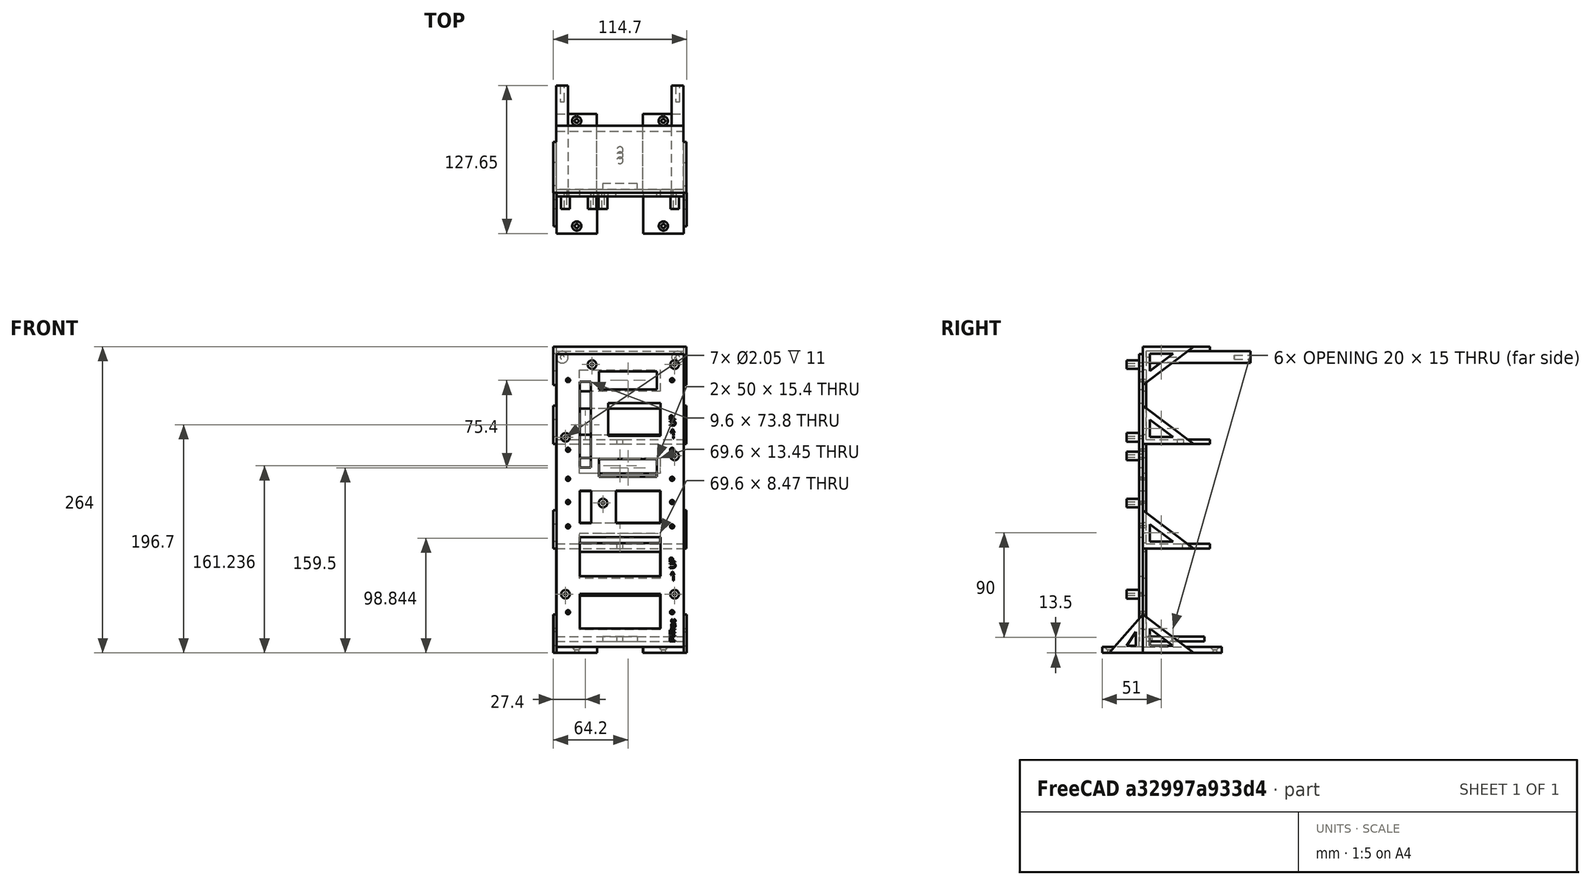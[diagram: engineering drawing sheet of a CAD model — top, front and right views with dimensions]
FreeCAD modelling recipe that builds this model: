
FCSTD DOCUMENT  (FreeCAD 1.0R39109 (Git))
Label: Tower
License: All rights reserved
LicenseURL: http://en.wikipedia.org/wiki/All_rights_reserved
objects: Sketcher::SketchObject×17, PartDesign::Pad×9, PartDesign::Plane×9, PartDesign::Pocket×5, PartDesign::Hole×3, PartDesign::Mirrored×2, PartDesign::Body×2, App::Link×1, Part::Part2DObjectPython×1, App::Part×1
note: 101 computed .brp shape members not serialized (recipe doc carries the construction recipe); baked Part::Feature solids carry a one-line shape summary decoded from their .brp
EXTERNAL_REF file=../Master Document.FCStd obj=Spreadsheet

FEATURE [App::Link] Link  label="Monitor Chassis Parameters"
  LinkedObject = -> <external ../Master Document.FCStd>#Spreadsheet
FEATURE [Sketcher::SketchObject] Sketch  label="Backplate Sketch"
  ArcFitTolerance = 1e-06
  AttachmentSupport = -> [XZ_Plane001]
  FullyConstrained = true
  MakeInternals = false
  MapMode = 5
  Placement = pos=(0,0,0) rot=(1,0,0;1.5708rad)
  expr: Constraints[107] = <<Monitor Chassis Parameters>>.GSBackPlateMinimumSpanWidth
  expr: Constraints[108] = <<Monitor Chassis Parameters>>.GSBackPlateMinimumSpanWidth - 8
  expr: Constraints[109] = <<Monitor Chassis Parameters>>.GSBackPlateMinimumSpanWidth - 5
  expr: Constraints[10] = <<Monitor Chassis Parameters>>.GSComputeBoardWidth / 2 - <<Monitor Chassis Parameters>>.GSBackPlateTopInnerHoleInsetFromSide
  expr: Constraints[118] = 30
  expr: Constraints[119] = <<Monitor Chassis Parameters>>.GSBackPlateMiddleRightHoleHeight
  expr: Constraints[11] = <<Monitor Chassis Parameters>>.GSBackPlateBoltDiameter
  expr: Constraints[120] = <<Monitor Chassis Parameters>>.GSBackPlateTopHolesHeight
  expr: Constraints[122] = <<Monitor Chassis Parameters>>.GSBackPlateMiddleHoleHeight
  expr: Constraints[123] = <<Monitor Chassis Parameters>>.GSBackPlateBottomHoleHeight
  expr: Constraints[126] = <<Monitor Chassis Parameters>>.GSBackPlateLengthIncrement
  expr: Constraints[12] = <<Monitor Chassis Parameters>>.GSComputeBoardWidth / 2 - <<Monitor Chassis Parameters>>.GSBackPlateOuterHolesInsetFromSide
  expr: Constraints[130] = <<Monitor Chassis Parameters>>.GSBackPlateMinimumSpanWidth
  expr: Constraints[131] = <<Monitor Chassis Parameters>>.GSBackPlateMinimumSpanWidth + 4
  expr: Constraints[132] = <<Monitor Chassis Parameters>>.GSBackPlateMinimumSpanWidth
  expr: Constraints[133] = <<Monitor Chassis Parameters>>.GSBackPlateMinimumSpanWidth - 5
  expr: Constraints[134] = <<Monitor Chassis Parameters>>.GSBackPlateWidth
  expr: Constraints[135] = <<Monitor Chassis Parameters>>.GSBackPlateHeight
  expr: Constraints[136] = <<Monitor Chassis Parameters>>.GSBackPlateMiddleLeftHoleHeight
  expr: Constraints[138] = <<Monitor Chassis Parameters>>.GSBackPlateBoltDiameter
  expr: Constraints[13] = <<Monitor Chassis Parameters>>.GSBackPlateBoltDiameter
  expr: Constraints[14] = <<Monitor Chassis Parameters>>.GSComputeBoardWidth / 2 - <<Monitor Chassis Parameters>>.GSBackPlateOuterHolesInsetFromSide
  expr: Constraints[150] = <<Monitor Chassis Parameters>>.GSBackPlateVerticalOffset
  expr: Constraints[15] = <<Monitor Chassis Parameters>>.GSBackPlateBoltDiameter
  expr: Constraints[17] = <<Monitor Chassis Parameters>>.GSComputeBoardWidth / 2 - <<Monitor Chassis Parameters>>.GSBackPlateOuterHolesInsetFromSide
  expr: Constraints[18] = <<Monitor Chassis Parameters>>.GSBackPlateBoltDiameter
  expr: Constraints[19] = <<Monitor Chassis Parameters>>.GSBackPlateWidth / 2 - <<Monitor Chassis Parameters>>.GSBackPlateMiddleHoleOffsetFromLeftSide
  expr: Constraints[20] = <<Monitor Chassis Parameters>>.GSBackPlateBoltDiameter
  expr: Constraints[21] = <<Monitor Chassis Parameters>>.GSBackPlateBoltDiameter
  expr: Constraints[25] = <<Monitor Chassis Parameters>>.GSBackPlateWidthIncrement
  expr: Constraints[66] = 50
  expr: Constraints[68] = 45
  expr: Constraints[73] = <<Monitor Chassis Parameters>>.GSBackPlateMinimumSpanWidth
  expr: Constraints[7] = <<Monitor Chassis Parameters>>.GSComputeBoardHeight
  expr: Constraints[82] = <<Monitor Chassis Parameters>>.GSBackPlateMinimumSpanWidth - 5
  expr: Constraints[8] = <<Monitor Chassis Parameters>>.GSComputeBoardWidth
  expr: Constraints[9] = <<Monitor Chassis Parameters>>.GSComputeBoardWidth / 2
  sketch-geometry (51):
    g0: LineSegment [constr] StartX=-50.8 StartY=20 StartZ=0 EndX=50.8 EndY=20 EndZ=0
    g1: LineSegment [constr] StartX=50.8 StartY=20 StartZ=0 EndX=50.8 EndY=248.6 EndZ=0
    g2: LineSegment [constr] StartX=50.8 StartY=248.6 StartZ=0 EndX=-50.8 EndY=248.6 EndZ=0
    g3: LineSegment [constr] StartX=-50.8 StartY=248.6 StartZ=0 EndX=-50.8 EndY=20 EndZ=0
    g4: Circle CenterX=-24.13 CenterY=243.52 CenterZ=0 NormalX=0 NormalY=0 NormalZ=1 AngleXU=0 Radius=1.4
    g5: Circle CenterX=46.99 CenterY=243.52 CenterZ=0 NormalX=0 NormalY=0 NormalZ=1 AngleXU=0 Radius=1.4
    g6: Circle CenterX=-46.99 CenterY=45.5 CenterZ=0 NormalX=0 NormalY=0 NormalZ=1 AngleXU=0 Radius=1.4
    g7: Circle CenterX=46.99 CenterY=45.5 CenterZ=0 NormalX=0 NormalY=0 NormalZ=1 AngleXU=0 Radius=1.4
    g8: Circle CenterX=-14.668 CenterY=124.14 CenterZ=0 NormalX=0 NormalY=0 NormalZ=1 AngleXU=0 Radius=1.4
    g9: Circle CenterX=-46.99 CenterY=180.78 CenterZ=0 NormalX=0 NormalY=0 NormalZ=1 AngleXU=0 Radius=1.4
    g10: Circle CenterX=46.99 CenterY=164.78 CenterZ=0 NormalX=0 NormalY=0 NormalZ=1 AngleXU=0 Radius=1.4
    g11: LineSegment StartX=-54.8 StartY=252.6 StartZ=0 EndX=-54.8 EndY=16 EndZ=0
    g12: LineSegment [constr] StartX=-54.8 StartY=16 StartZ=0 EndX=54.8 EndY=16 EndZ=0
    g13: LineSegment StartX=31.8 StartY=162.2 StartZ=0 EndX=-18.2 EndY=162.2 EndZ=0
    g14: LineSegment StartX=-18.2 StartY=162.2 StartZ=0 EndX=-18.2 EndY=146.8 EndZ=0
    g15: LineSegment StartX=-18.2 StartY=146.8 StartZ=0 EndX=31.8 EndY=146.8 EndZ=0
    g16: LineSegment StartX=31.8 StartY=146.8 StartZ=0 EndX=31.8 EndY=162.2 EndZ=0
    g17: LineSegment StartX=34.8 StartY=106.8 StartZ=0 EndX=-3.7 EndY=106.8 EndZ=0
    g18: LineSegment StartX=-3.7 StartY=106.8 StartZ=0 EndX=-3.7 EndY=134.8 EndZ=0
    g19: LineSegment StartX=-3.7 StartY=134.8 StartZ=0 EndX=34.8 EndY=134.8 EndZ=0
    g20: LineSegment StartX=34.8 StartY=134.8 StartZ=0 EndX=34.8 EndY=106.8 EndZ=0
    g21: LineSegment StartX=31.8 StartY=237.6 StartZ=0 EndX=-18.2 EndY=237.6 EndZ=0
    g22: LineSegment StartX=-18.2 StartY=237.6 StartZ=0 EndX=-18.2 EndY=222.2 EndZ=0
    g23: LineSegment StartX=-18.2 StartY=222.2 StartZ=0 EndX=31.8 EndY=222.2 EndZ=0
    g24: LineSegment StartX=31.8 StartY=222.2 StartZ=0 EndX=31.8 EndY=237.6 EndZ=0
    g25: LineSegment StartX=34.8 StartY=182.2 StartZ=0 EndX=-10.2 EndY=182.2 EndZ=0
    g26: LineSegment StartX=-10.2 StartY=182.2 StartZ=0 EndX=-10.2 EndY=210.2 EndZ=0
    g27: LineSegment StartX=-10.2 StartY=210.2 StartZ=0 EndX=34.8 EndY=210.2 EndZ=0
    g28: LineSegment StartX=34.8 StartY=210.2 StartZ=0 EndX=34.8 EndY=182.2 EndZ=0
    g29: LineSegment StartX=-34.8 StartY=228.6 StartZ=0 EndX=-34.8 EndY=154.8 EndZ=0
    g30: LineSegment StartX=-34.8 StartY=154.8 StartZ=0 EndX=-25.2 EndY=154.8 EndZ=0
    g31: LineSegment StartX=-25.2 StartY=154.8 StartZ=0 EndX=-25.2 EndY=228.6 EndZ=0
    g32: LineSegment StartX=-25.2 StartY=228.6 StartZ=0 EndX=-34.8 EndY=228.6 EndZ=0
    g33: LineSegment StartX=-34.8 StartY=134.8 StartZ=0 EndX=-34.8 EndY=106.8 EndZ=0
    g34: LineSegment StartX=-34.8 StartY=106.8 StartZ=0 EndX=-24.668 EndY=106.8 EndZ=0
    g35: LineSegment StartX=-24.668 StartY=106.8 StartZ=0 EndX=-24.668 EndY=134.8 EndZ=0
    g36: LineSegment StartX=-24.668 StartY=134.8 StartZ=0 EndX=-34.8 EndY=134.8 EndZ=0
    g37: LineSegment StartX=-34.8 StartY=94.8 StartZ=0 EndX=-34.8 EndY=61 EndZ=0
    g38: LineSegment StartX=-34.8 StartY=61 StartZ=0 EndX=34.8 EndY=61 EndZ=0
    g39: LineSegment StartX=34.8 StartY=61 StartZ=0 EndX=34.8 EndY=94.8 EndZ=0
    g40: LineSegment StartX=34.8 StartY=94.8 StartZ=0 EndX=-34.8 EndY=94.8 EndZ=0
    g41: LineSegment StartX=-34.8 StartY=46 StartZ=0 EndX=-34.8 EndY=16 EndZ=0
    g42: LineSegment StartX=-34.8 StartY=16 StartZ=0 EndX=34.8 EndY=16 EndZ=0
    g43: LineSegment StartX=34.8 StartY=16 StartZ=0 EndX=34.8 EndY=46 EndZ=0
    g44: LineSegment StartX=34.8 StartY=46 StartZ=0 EndX=-34.8 EndY=46 EndZ=0
    g45: LineSegment StartX=54.8 StartY=16 StartZ=0 EndX=54.8 EndY=252.6 EndZ=0
    g46: LineSegment StartX=-54.8 StartY=252.6 StartZ=0 EndX=54.8 EndY=252.6 EndZ=0
    g47: LineSegment StartX=-54.8 StartY=16 StartZ=0 EndX=-54.8 EndY=0 EndZ=0
    g48: LineSegment StartX=-54.8 StartY=0 StartZ=0 EndX=54.8 EndY=0 EndZ=0
    g49: LineSegment StartX=54.8 StartY=0 StartZ=0 EndX=54.8 EndY=16 EndZ=0
    g50: LineSegment [constr] StartX=54.8 StartY=16 StartZ=0 EndX=-54.8 EndY=16 EndZ=0
  constraints (152):
    c: Coincident(g0,g1)
    c: Coincident(g1,g2)
    c: Coincident(g2,g3)
    c: Coincident(g3,g0)
    c: Horizontal(g2)
    c: Vertical(g1)
    c: Vertical(g3)
    c: DistanceY(g0,g2) = 228.6
    c: DistanceX(g0,g0) = 101.6
    c: DistanceX(g0,g-1) = 50.8
    c: DistanceX(g4,g-1) = 24.13
    c: Diameter(g4) = 2.8
    c: DistanceX(g-1,g5) = 46.99
    c: Diameter(g6) = 2.8
    c: DistanceX(g6,g-1) = 46.99
    c: Diameter(g7) = 2.8
    c: Horizontal(g7,g6)
    c: DistanceX(g-1,g7) = 46.99
    c: Diameter(g8) = 2.8
    c: DistanceX(g8,g-1) = 14.668
    c: Diameter(g9) = 2.8
    c: Diameter(g10) = 2.8
    c: Coincident(g11,g12)
    c: Vertical(g11)
    c: Horizontal(g12)
    c: DistanceX(g11,g0) = 4
    c: Horizontal(g0)
    c: Vertical(g6,g9)
    c: Coincident(g13,g14)
    c: Coincident(g14,g15)
    c: Coincident(g15,g16)
    c: Coincident(g16,g13)
    c: Horizontal(g13)
    c: Horizontal(g15)
    c: Vertical(g14)
    c: Vertical(g16)
    c: Coincident(g17,g18)
    c: Coincident(g18,g19)
    c: Coincident(g19,g20)
    c: Coincident(g20,g17)
    c: Horizontal(g17)
    c: Horizontal(g19)
    c: Vertical(g18)
    c: Vertical(g20)
    c: DistanceX(g13,g13) = 50
    c: DistanceY(g14,g13) = 15.4
    c: DistanceX(g18,g19) = 38.5
    c: DistanceY(g17,g18) = 28
    c: DistanceY(g19,g15) = 12
    c: DistanceX(g15,g19) = 3
    c: Coincident(g21,g22)
    c: Coincident(g22,g23)
    c: Coincident(g23,g24)
    c: Coincident(g24,g21)
    c: Horizontal(g21)
    c: Horizontal(g23)
    c: Vertical(g22)
    c: Vertical(g24)
    c: Coincident(g25,g26)
    c: Coincident(g26,g27)
    c: Coincident(g27,g28)
    c: Coincident(g28,g25)
    c: Horizontal(g25)
    c: Horizontal(g27)
    c: Vertical(g26)
    c: Vertical(g28)
    c: DistanceX(g21,g21) = 50
    c: DistanceY(g22,g21) = 15.4
    c: DistanceX(g26,g27) = 45
    c: DistanceY(g25,g26) = 28
    c: DistanceY(g27,g23) = 12
    c: DistanceX(g23,g27) = 3
    c: Vertical(g19,g25)
    c: DistanceY(g13,g25) = 20
    c: Coincident(g29,g30)
    c: Coincident(g30,g31)
    c: Coincident(g31,g32)
    c: Coincident(g32,g29)
    c: Vertical(g29)
    c: Vertical(g31)
    c: Horizontal(g30)
    c: Horizontal(g32)
    c: DistanceX(g31,g26) = 15
    c: Coincident(g33,g34)
    c: Coincident(g34,g35)
    c: Coincident(g35,g36)
    c: Coincident(g36,g33)
    c: Vertical(g33)
    c: Vertical(g35)
    c: Horizontal(g34)
    c: Horizontal(g36)
    c: Coincident(g37,g38)
    c: Coincident(g38,g39)
    c: Coincident(g39,g40)
    c: Coincident(g40,g37)
    c: Vertical(g37)
    c: Vertical(g39)
    c: Horizontal(g38)
    c: Horizontal(g40)
    c: Coincident(g41,g42)
    c: Coincident(g42,g43)
    c: Coincident(g43,g44)
    c: Coincident(g44,g41)
    c: Vertical(g41)
    c: Vertical(g43)
    c: Horizontal(g42)
    c: Horizontal(g44)
    c: DistanceY(g33,g29) = 20
    c: DistanceY(g37,g33) = 12
    c: DistanceY(g41,g37) = 15
    c: Vertical(g29,g33)
    c: Vertical(g33,g37)
    c: Vertical(g37,g41)
    c: Vertical(g17,g39)
    c: Vertical(g39,g43)
    c: Horizontal(g35,g18)
    c: DistanceX(g35,g8) = 10
    c: Horizontal(g34,g17)
    c: DistanceY(g41,g41) = 30
    c: DistanceY(g0,g10) = 144.78
    c: DistanceY(g0,g4) = 223.52
    c: Horizontal(g5,g4)
    c: DistanceY(g0,g8) = 104.14
    c: DistanceY(g0,g6) = 25.5
    c: Coincident(g45,g12)
    c: Vertical(g45)
    c: DistanceY(g1,g45) = 4
    c: Horizontal(g11,g45)
    c: Coincident(g46,g11)
    c: Coincident(g46,g45)
    c: DistanceX(g11,g29) = 20
    c: DistanceY(g29,g11) = 24
    c: DistanceX(g27,g45) = 20
    c: DistanceY(g21,g45) = 15
    c: DistanceX(g11,g12) = 109.6
    c: DistanceY(g11,g11) = 236.6
    c: DistanceY(g0,g9) = 160.78
    c: Vertical(g7,g10)
    c: Diameter(g5) = 2.8
    c: Coincident(g47,g48)
    c: Coincident(g48,g49)
    c: Coincident(g49,g50)
    c: Coincident(g50,g47)
    c: Vertical(g47)
    c: Vertical(g49)
    c: Horizontal(g48)
    c: Horizontal(g50)
    c: Coincident(g47,g11)
    c: Horizontal(g48,g-1)
    c: Vertical(g49,g12)
    c: DistanceY(g-1,g0) = 20
    c: Horizontal(g41,g11)
FEATURE [PartDesign::Pad] Pad  label="Backplate Pad"
  Direction = (0,-1,2e-16)
  Length = 3
  Length2 = 10
  Placement = pos=(0,0,0) rot=(1,0,0;1.5708rad)
  Profile = -> Sketch
  ReferenceAxis = -> Sketch [N_Axis]
  Reversed = true
  Suppressed = false
  Type = 0
  expr: Length = <<Monitor Chassis Parameters>>.GSBackPlateThickness
FEATURE [Sketcher::SketchObject] Sketch001  label="Backplate Risers Sketch"
  ArcFitTolerance = 1e-06
  AttachmentSupport = -> [XZ_Plane001]
  FullyConstrained = true
  MakeInternals = false
  MapMode = 5
  Placement = pos=(0,0,0) rot=(1,0,0;1.5708rad)
  expr: Constraints[10] = <<Monitor Chassis Parameters>>.GSM2_5TappingScrewHoleDiameter
  expr: Constraints[11] = <<Monitor Chassis Parameters>>.GSM2_5TappingScrewHoleDiameter
  expr: Constraints[12] = <<Monitor Chassis Parameters>>.GSComputeBoardWidth / 2 - <<Monitor Chassis Parameters>>.GSBackPlateOuterHolesInsetFromSide
  expr: Constraints[13] = <<Monitor Chassis Parameters>>.GSM2_5TappingScrewHoleDiameter
  expr: Constraints[14] = <<Monitor Chassis Parameters>>.GSComputeBoardWidth / 2 - <<Monitor Chassis Parameters>>.GSBackPlateOuterHolesInsetFromSide
  expr: Constraints[15] = <<Monitor Chassis Parameters>>.GSM2_5TappingScrewHoleDiameter
  expr: Constraints[16] = <<Monitor Chassis Parameters>>.GSComputeBoardWidth / 2 - <<Monitor Chassis Parameters>>.GSBackPlateOuterHolesInsetFromSide
  expr: Constraints[17] = <<Monitor Chassis Parameters>>.GSM2_5TappingScrewHoleDiameter
  expr: Constraints[18] = <<Monitor Chassis Parameters>>.GSBackPlateWidth / 2 - <<Monitor Chassis Parameters>>.GSBackPlateMiddleHoleOffsetFromLeftSide
  expr: Constraints[19] = <<Monitor Chassis Parameters>>.GSM2_5TappingScrewHoleDiameter
  expr: Constraints[20] = <<Monitor Chassis Parameters>>.GSM2_5TappingScrewHoleDiameter
  expr: Constraints[25] = <<Monitor Chassis Parameters>>.GSBackPlateScrewHoleDiameter + 2 * <<Monitor Chassis Parameters>>.GSBackPlateStandoffWallThickness
  expr: Constraints[27] = <<Monitor Chassis Parameters>>.GSBackPlateScrewHoleDiameter + 2 * <<Monitor Chassis Parameters>>.GSBackPlateStandoffWallThickness
  expr: Constraints[33] = <<Monitor Chassis Parameters>>.GSBackPlateScrewHoleDiameter + 2 * <<Monitor Chassis Parameters>>.GSBackPlateStandoffWallThickness
  expr: Constraints[34] = <<Monitor Chassis Parameters>>.GSBackPlateScrewHoleDiameter + 2 * <<Monitor Chassis Parameters>>.GSBackPlateStandoffWallThickness
  expr: Constraints[35] = <<Monitor Chassis Parameters>>.GSBackPlateScrewHoleDiameter + 2 * <<Monitor Chassis Parameters>>.GSBackPlateStandoffWallThickness
  expr: Constraints[36] = <<Monitor Chassis Parameters>>.GSBackPlateScrewHoleDiameter + 2 * <<Monitor Chassis Parameters>>.GSBackPlateStandoffWallThickness
  expr: Constraints[37] = <<Monitor Chassis Parameters>>.GSBackPlateScrewHoleDiameter + 2 * <<Monitor Chassis Parameters>>.GSBackPlateStandoffWallThickness
  expr: Constraints[39] = <<Monitor Chassis Parameters>>.GSBackPlateMiddleLeftHoleHeight
  expr: Constraints[40] = <<Monitor Chassis Parameters>>.GSBackPlateBottomHoleHeight
  expr: Constraints[42] = <<Monitor Chassis Parameters>>.GSBackPlateMiddleHoleHeight
  expr: Constraints[43] = <<Monitor Chassis Parameters>>.GSBackPlateTopHolesHeight
  expr: Constraints[44] = <<Monitor Chassis Parameters>>.GSBackPlateMiddleRightHoleHeight
  expr: Constraints[45] = <<Monitor Chassis Parameters>>.GSBackPlateVerticalOffset
  expr: Constraints[6] = <<Monitor Chassis Parameters>>.GSComputeBoardHeight
  expr: Constraints[7] = <<Monitor Chassis Parameters>>.GSComputeBoardWidth
  expr: Constraints[8] = <<Monitor Chassis Parameters>>.GSComputeBoardWidth / 2
  expr: Constraints[9] = 0.5 * <<Monitor Chassis Parameters>>.GSComputeBoardWidth - <<Monitor Chassis Parameters>>.GSBackPlateTopInnerHoleInsetFromSide
  sketch-geometry (18):
    g0: LineSegment [constr] StartX=-50.8 StartY=20 StartZ=0 EndX=50.8 EndY=20 EndZ=0
    g1: LineSegment [constr] StartX=50.8 StartY=20 StartZ=0 EndX=50.8 EndY=248.6 EndZ=0
    g2: LineSegment [constr] StartX=50.8 StartY=248.6 StartZ=0 EndX=-50.8 EndY=248.6 EndZ=0
    g3: LineSegment [constr] StartX=-50.8 StartY=248.6 StartZ=0 EndX=-50.8 EndY=20 EndZ=0
    g4: Circle CenterX=-24.13 CenterY=243.52 CenterZ=0 NormalX=0 NormalY=0 NormalZ=1 AngleXU=0 Radius=1.025
    g5: Circle CenterX=46.99 CenterY=243.52 CenterZ=0 NormalX=0 NormalY=0 NormalZ=1 AngleXU=0 Radius=1.025
    g6: Circle CenterX=-46.99 CenterY=45.5 CenterZ=0 NormalX=0 NormalY=0 NormalZ=1 AngleXU=0 Radius=1.025
    g7: Circle CenterX=46.99 CenterY=45.5 CenterZ=0 NormalX=0 NormalY=0 NormalZ=1 AngleXU=0 Radius=1.025
    g8: Circle CenterX=-14.668 CenterY=124.14 CenterZ=0 NormalX=0 NormalY=0 NormalZ=1 AngleXU=0 Radius=1.025
    g9: Circle CenterX=-46.99 CenterY=180.78 CenterZ=0 NormalX=0 NormalY=0 NormalZ=1 AngleXU=0 Radius=1.025
    g10: Circle CenterX=46.99 CenterY=164.78 CenterZ=0 NormalX=0 NormalY=0 NormalZ=1 AngleXU=0 Radius=1.025
    g11: Circle CenterX=-24.13 CenterY=243.52 CenterZ=0 NormalX=0 NormalY=0 NormalZ=1 AngleXU=0 Radius=3.7
    g12: Circle CenterX=46.99 CenterY=243.52 CenterZ=0 NormalX=0 NormalY=0 NormalZ=1 AngleXU=0 Radius=3.7
    g13: Circle CenterX=-46.99 CenterY=180.78 CenterZ=0 NormalX=0 NormalY=0 NormalZ=1 AngleXU=0 Radius=3.7
    g14: Circle CenterX=46.99 CenterY=164.78 CenterZ=0 NormalX=0 NormalY=0 NormalZ=1 AngleXU=0 Radius=3.7
    g15: Circle CenterX=-14.668 CenterY=124.14 CenterZ=0 NormalX=0 NormalY=0 NormalZ=1 AngleXU=0 Radius=3.7
    g16: Circle CenterX=-46.99 CenterY=45.5 CenterZ=0 NormalX=0 NormalY=0 NormalZ=1 AngleXU=0 Radius=3.7
    g17: Circle CenterX=46.99 CenterY=45.5 CenterZ=0 NormalX=0 NormalY=0 NormalZ=1 AngleXU=0 Radius=3.7
  constraints (47):
    c: Coincident(g0,g1)
    c: Coincident(g1,g2)
    c: Coincident(g2,g3)
    c: Coincident(g3,g0)
    c: Vertical(g1)
    c: Vertical(g3)
    c: DistanceY(g0,g2) = 228.6
    c: DistanceX(g0,g0) = 101.6
    c: DistanceX(g0,g-1) = 50.8
    c: DistanceX(g4,g-1) = 24.13
    c: Diameter(g4) = 2.05
    c: Diameter(g5) = 2.05
    c: DistanceX(g-1,g5) = 46.99
    c: Diameter(g6) = 2.05
    c: DistanceX(g6,g-1) = 46.99
    c: Diameter(g7) = 2.05
    c: DistanceX(g-1,g7) = 46.99
    c: Diameter(g8) = 2.05
    c: DistanceX(g8,g-1) = 14.668
    c: Diameter(g9) = 2.05
    c: Diameter(g10) = 2.05
    c: Horizontal(g0)
    c: Vertical(g5,g10)
    c: Horizontal(g5,g4)
    c: Coincident(g11,g4)
    c: Diameter(g11) = 7.4
    c: Coincident(g12,g5)
    c: Diameter(g12) = 7.4
    c: Coincident(g13,g9)
    c: Coincident(g14,g10)
    c: Coincident(g15,g8)
    c: Coincident(g16,g6)
    c: Coincident(g17,g7)
    c: Diameter(g17) = 7.4
    c: Diameter(g16) = 7.4
    c: Diameter(g15) = 7.4
    c: Diameter(g14) = 7.4
    c: Diameter(g13) = 7.4
    c: Vertical(g9,g6)
    c: DistanceY(g0,g9) = 160.78
    c: DistanceY(g0,g6) = 25.5
    c: Horizontal(g7,g6)
    c: DistanceY(g0,g8) = 104.14
    c: DistanceY(g0,g4) = 223.52
    c: DistanceY(g0,g10) = 144.78
    c: DistanceY(g-1,g0) = 20
    c: Horizontal(g2,g1)
FEATURE [PartDesign::Pad] Pad001  label="Backplate Risers Pad"
  BaseFeature = -> Pad
  Direction = (0,-1,2e-16)
  Length = 11
  Length2 = 10
  Placement = pos=(0,0,0) rot=(1,0,0;1.5708rad)
  Profile = -> Sketch001
  ReferenceAxis = -> Sketch001 [N_Axis]
  Suppressed = false
  Type = 0
  expr: Length = <<Monitor Chassis Parameters>>.GSBackPlateStandoffHeight
FEATURE [Sketcher::SketchObject] Sketch002  label="Backplate Foot Sketch"
  ArcFitTolerance = 1e-06
  AttachmentSupport = -> [XZ_Plane001]
  FullyConstrained = true
  MakeInternals = false
  MapMode = 5
  Placement = pos=(0,0,0) rot=(1,0,0;1.5708rad)
  expr: Constraints[11] = <<Monitor Chassis Parameters>>.GSTowerFeetThickness
  expr: Constraints[21] = <<Monitor Chassis Parameters>>.GSTowerFeetThickness
  expr: Constraints[22] = <<Monitor Chassis Parameters>>.GSBackPlateFootWidth
  expr: Constraints[23] = 0.5 * <<Monitor Chassis Parameters>>.GSBackPlateWidth
  expr: Constraints[8] = <<Monitor Chassis Parameters>>.GSBackPlateFootWidth
  expr: Constraints[9] = 0.5 * <<Monitor Chassis Parameters>>.GSBackPlateWidth
  sketch-geometry (8):
    g0: LineSegment StartX=-54.8 StartY=-5 StartZ=0 EndX=-19.8 EndY=-5 EndZ=0
    g1: LineSegment StartX=-19.8 StartY=-5 StartZ=0 EndX=-19.8 EndY=0 EndZ=0
    g2: LineSegment StartX=-19.8 StartY=0 StartZ=0 EndX=-54.8 EndY=0 EndZ=0
    g3: LineSegment StartX=-54.8 StartY=0 StartZ=0 EndX=-54.8 EndY=-5 EndZ=0
    g4: LineSegment StartX=54.8 StartY=-5 StartZ=0 EndX=54.8 EndY=0 EndZ=0
    g5: LineSegment StartX=54.8 StartY=0 StartZ=0 EndX=19.8 EndY=0 EndZ=0
    g6: LineSegment StartX=19.8 StartY=0 StartZ=0 EndX=19.8 EndY=-5 EndZ=0
    g7: LineSegment StartX=19.8 StartY=-5 StartZ=0 EndX=54.8 EndY=-5 EndZ=0
  constraints (24):
    c: Coincident(g0,g1)
    c: Coincident(g1,g2)
    c: Coincident(g2,g3)
    c: Coincident(g3,g0)
    c: Horizontal(g0)
    c: Horizontal(g2)
    c: Vertical(g1)
    c: Vertical(g3)
    c: DistanceX(g2,g1) = 35
    c: DistanceX(g2,g-1) = 54.8
    c: Horizontal(g2,g-1)
    c: DistanceY(g0,g2) = 5
    c: Coincident(g4,g5)
    c: Coincident(g5,g6)
    c: Coincident(g6,g7)
    c: Coincident(g7,g4)
    c: Vertical(g4)
    c: Vertical(g6)
    c: Horizontal(g5)
    c: Horizontal(g7)
    c: Horizontal(g5,g-1)
    c: DistanceY(g4,g4) = 5
    c: DistanceX(g6,g4) = 35
    c: DistanceX(g-1,g4) = 54.8
FEATURE [PartDesign::Pad] Pad002  label="Backplate Foot Pad"
  BaseFeature = -> Pad001
  Direction = (0,-1,2e-16)
  Length = 32
  Length2 = 3
  Placement = pos=(0,0,0) rot=(1,0,0;1.5708rad)
  Profile = -> Sketch002
  ReferenceAxis = -> Sketch002 [N_Axis]
  Suppressed = false
  Type = 4
  expr: Length = <<Monitor Chassis Parameters>>.GSBackPlateFootLengthBackward
  expr: Length2 = <<Monitor Chassis Parameters>>.GSBackPlateThickness
FEATURE [Sketcher::SketchObject] Sketch003  label="Backplate Foot Screw Holes Sketch"
  ArcFitTolerance = 1e-06
  AttachmentSupport = -> [XY_Plane001]
  FullyConstrained = true
  MakeInternals = false
  MapMode = 5
  expr: Constraints[0] = 0.8 * <<Monitor Chassis Parameters>>.GSBackPlateFootLengthBackward
  expr: Constraints[1] = 0.5 * <<Monitor Chassis Parameters>>.GSBackPlateWidth - 0.5 * <<Monitor Chassis Parameters>>.GSBackPlateFootWidth
  expr: Constraints[2] = 0.5 * <<Monitor Chassis Parameters>>.GSBackPlateWidth - 0.5 * <<Monitor Chassis Parameters>>.GSBackPlateFootWidth
  expr: Constraints[3] = <<Monitor Chassis Parameters>>.GSTowerFeetScrewDiameter
  expr: Constraints[4] = <<Monitor Chassis Parameters>>.GSTowerFeetScrewDiameter
  sketch-geometry (2):
    g0: Circle CenterX=-37.3 CenterY=-25.6 CenterZ=0 NormalX=0 NormalY=0 NormalZ=1 AngleXU=0 Radius=1.7
    g1: Circle CenterX=37.3 CenterY=-25.6 CenterZ=0 NormalX=0 NormalY=0 NormalZ=1 AngleXU=0 Radius=1.7
  constraints (6):
    c: DistanceY(g0,g-1) = 25.6
    c: DistanceX(g0,g-1) = 37.3
    c: DistanceX(g-1,g1) = 37.3
    c: Diameter(g0) = 3.4
    c: Diameter(g1) = 3.4
    c: Horizontal(g1,g0)
FEATURE [PartDesign::Hole] Hole  label="Backplate Foot Screw Holes"
  BaseFeature = -> Pad002
  CustomThreadClearance = 0
  Depth = 25
  DepthType = 0
  Diameter = 3.4
  DrillForDepth = false
  DrillPoint = 1
  DrillPointAngle = 118
  HoleCutCountersinkAngle = 90
  HoleCutCustomValues = false
  HoleCutDepth = 0
  HoleCutDiameter = 8
  HoleCutType = 2
  ModelThread = false
  Placement = pos=(0,0,0) rot=(1,0,0;1.5708rad)
  Profile = -> Sketch003
  Suppressed = false
  Tapered = false
  TaperedAngle = 90
  ThreadClass = 0
  ThreadDepth = 25
  ThreadDepthType = 0
  ThreadDirection = 0
  ThreadFit = 0
  ThreadSize = 0
  ThreadType = 0
  Threaded = false
  UseCustomThreadClearance = false
  expr: Diameter = <<Monitor Chassis Parameters>>.GSTowerFeetScrewDiameter
  expr: HoleCutDiameter = <<Monitor Chassis Parameters>>.GSM4BoltCountersinkDiameter
FEATURE [PartDesign::Plane] DatumPlane
  AttachmentOffset = pos=(0,0,54.8) rot=(0,0,1;0rad)
  AttachmentSupport = -> [YZ_Plane001]
  Length = 60
  MapMode = 5
  Placement = pos=(54.8,0,0) rot=(0.57735,0.57735,0.57735;2.0944rad)
  ResizeMode = 0
  Width = 60
  expr: .AttachmentOffset.Base.z = 0.5 * <<Monitor Chassis Parameters>>.GSBackPlateWidth
FEATURE [Sketcher::SketchObject] Sketch004  label="Foot Support Corner Sketch"
  ArcFitTolerance = 1e-06
  AttachmentSupport = -> [DatumPlane]
  FullyConstrained = true
  MakeInternals = false
  MapMode = 5
  Placement = pos=(54.8,0,0) rot=(0.57735,0.57735,0.57735;2.0944rad)
  expr: Constraints[14] = <<Monitor Chassis Parameters>>.GSSideCornerCutoutInset
  expr: Constraints[15] = <<Monitor Chassis Parameters>>.GSSideCornerCutoutInset
  expr: Constraints[16] = 2.5 * <<Monitor Chassis Parameters>>.GSSideCornerCutoutInset
  expr: Constraints[17] = 2.5 * <<Monitor Chassis Parameters>>.GSSideCornerCutoutInset
  expr: Constraints[1] = <<Monitor Chassis Parameters>>.GSBackPlateThickness
  expr: Constraints[4] = <<Monitor Chassis Parameters>>.GSTowerFeetThickness
  expr: Constraints[7] = 0.9 * <<Monitor Chassis Parameters>>.GSBackPlateFootLengthBackward
  expr: Constraints[8] = 0.6 * <<Monitor Chassis Parameters>>.GSTowerFloorDepth
  sketch-geometry (6):
    g0: LineSegment StartX=-25.8 StartY=-5 StartZ=0 EndX=3 EndY=-5 EndZ=0
    g1: LineSegment StartX=3 StartY=28 StartZ=0 EndX=3 EndY=-5 EndZ=0
    g2: LineSegment StartX=-25.8 StartY=-5 StartZ=0 EndX=3 EndY=28 EndZ=0
    g3: LineSegment StartX=-10.8 StartY=1 StartZ=0 EndX=-3 EndY=13 EndZ=0
    g4: LineSegment StartX=-3 StartY=13 StartZ=0 EndX=-3 EndY=1 EndZ=0
    g5: LineSegment StartX=-10.8 StartY=1 StartZ=0 EndX=-3 EndY=1 EndZ=0
  constraints (18):
    c: Horizontal(g0)
    c: DistanceX(g-1,g0) = 3
    c: Coincident(g1,g0)
    c: Vertical(g1)
    c: DistanceY(g0,g-1) = 5
    c: Coincident(g2,g0)
    c: Coincident(g2,g1)
    c: DistanceX(g0,g0) = 28.8
    c: DistanceY(g0,g1) = 33
    c: Coincident(g4,g3)
    c: Vertical(g4)
    c: Coincident(g5,g3)
    c: Coincident(g5,g4)
    c: Horizontal(g5)
    c: DistanceY(g0,g4) = 6
    c: DistanceX(g4,g0) = 6
    c: DistanceX(g0,g3) = 15
    c: DistanceY(g3,g1) = 15
FEATURE [PartDesign::Pad] Pad003  label="Foot Support Corner Pad"
  BaseFeature = -> Hole
  Direction = (1,0,0)
  Length = 2.5
  Length2 = 10
  Placement = pos=(0,0,0) rot=(1,0,0;1.5708rad)
  Profile = -> Sketch004
  ReferenceAxis = -> Sketch004 [N_Axis]
  Suppressed = false
  Type = 0
  expr: Length = <<Monitor Chassis Parameters>>.GSSideCornerThickness
FEATURE [PartDesign::Mirrored] Mirrored  label="Foot Support Corner Mirrored"
  BaseFeature = -> Pad003
  MirrorPlane = -> YZ_Plane001
  Originals = -> [Pad003]
  Placement = pos=(0,0,0) rot=(1,0,0;1.5708rad)
  Suppressed = false
  TransformMode = 0
FEATURE [PartDesign::Plane] DatumPlane001
  AttachmentOffset = pos=(0,0,54.8) rot=(0,0,1;0rad)
  AttachmentSupport = -> [YZ_Plane002]
  Length = 60
  MapMode = 5
  Placement = pos=(54.8,0,0) rot=(0.57735,0.57735,0.57735;2.0944rad)
  ResizeMode = 0
  Width = 60
  expr: .AttachmentOffset.Base.z = 0.5 * <<Monitor Chassis Parameters>>.GSBackPlateWidth
FEATURE [Sketcher::SketchObject] Sketch005  label="Frontplate Sketch"
  ArcFitTolerance = 1e-06
  AttachmentSupport = -> [XZ_Plane002]
  FullyConstrained = false
  MakeInternals = false
  MapMode = 5
  Placement = pos=(0,0,0) rot=(1,0,0;1.5708rad)
  expr: Constraints[105] = <<Monitor Chassis Parameters>>.GSFrontPlateMinimumSpanWidth - 5
  expr: Constraints[106] = <<Monitor Chassis Parameters>>.GSTowerFourthFloorHeight + <<Monitor Chassis Parameters>>.GSTowerFloorThickness
  expr: Constraints[107] = <<Monitor Chassis Parameters>>.GSTowerLayerJoinScrewDiameter
  expr: Constraints[108] = <<Monitor Chassis Parameters>>.GSTowerLayerJoinScrewDiameter
  expr: Constraints[110] = <<Monitor Chassis Parameters>>.GSTowerLayerJoinScrewInset
  expr: Constraints[111] = <<Monitor Chassis Parameters>>.GSTowerLayerJoinScrewInset
  expr: Constraints[112] = <<Monitor Chassis Parameters>>.GSTowerLayerJoinScrewDiameter
  expr: Constraints[113] = <<Monitor Chassis Parameters>>.GSTowerLayerJoinScrewDiameter
  expr: Constraints[115] = <<Monitor Chassis Parameters>>.GSTowerLayerJoinScrewDiameter
  expr: Constraints[116] = <<Monitor Chassis Parameters>>.GSTowerLayerJoinScrewDiameter
  expr: Constraints[120] = <<Monitor Chassis Parameters>>.GSTowerLayerJoinScrewDiameter
  expr: Constraints[121] = <<Monitor Chassis Parameters>>.GSTowerLayerJoinScrewDiameter
  expr: Constraints[123] = <<Monitor Chassis Parameters>>.GSTowerLayerJoinScrewHeightFromFoot_1
  expr: Constraints[124] = <<Monitor Chassis Parameters>>.GSTowerLayerJoinScrewHeightFromFoot_3
  expr: Constraints[126] = <<Monitor Chassis Parameters>>.GSTowerLayerJoinScrewHeightFromFoot_4
  expr: Constraints[127] = <<Monitor Chassis Parameters>>.GSTowerLayerJoinScrewHeightFromFoot_5
  expr: Constraints[129] = <<Monitor Chassis Parameters>>.GSTowerLayerJoinScrewDiameter
  expr: Constraints[130] = <<Monitor Chassis Parameters>>.GSTowerLayerJoinScrewDiameter
  expr: Constraints[133] = <<Monitor Chassis Parameters>>.GSTowerLayerJoinScrewHeightFromFoot_6
  expr: Constraints[13] = <<Monitor Chassis Parameters>>.GSBackPlateWidthIncrement
  expr: Constraints[145] = <<Monitor Chassis Parameters>>.GSTowerLayerJoinScrewDiameter
  expr: Constraints[150] = <<Monitor Chassis Parameters>>.GSTowerLayerJoinScrewHeightFromFoot_2
  expr: Constraints[46] = <<Monitor Chassis Parameters>>.GSFrontPlateMinimumSpanWidth - 5
  expr: Constraints[48] = <<Monitor Chassis Parameters>>.GSFrontPlateMinimumSpanWidth
  expr: Constraints[65] = <<Monitor Chassis Parameters>>.GSFrontPlateMinimumSpanWidth - 5
  expr: Constraints[71] = <<Monitor Chassis Parameters>>.GSBackPlateLengthIncrement
  expr: Constraints[75] = <<Monitor Chassis Parameters>>.GSBackPlateWidth
  expr: Constraints[76] = <<Monitor Chassis Parameters>>.GSBackPlateVerticalOffset
  expr: Constraints[7] = <<Monitor Chassis Parameters>>.GSComputeBoardHeight
  expr: Constraints[8] = <<Monitor Chassis Parameters>>.GSComputeBoardWidth
  expr: Constraints[96] = <<Monitor Chassis Parameters>>.GSFrontPlateMinimumSpanWidth - 5
  expr: Constraints[97] = <<Monitor Chassis Parameters>>.GSFrontPlateMinimumSpanWidth
  expr: Constraints[98] = <<Monitor Chassis Parameters>>.GSFrontPlateMinimumSpanWidth
  expr: Constraints[9] = <<Monitor Chassis Parameters>>.GSComputeBoardWidth / 2
  sketch-geometry (55):
    g0: LineSegment [constr] StartX=-50.8 StartY=24 StartZ=0 EndX=50.8 EndY=24 EndZ=0
    g1: LineSegment [constr] StartX=50.8 StartY=24 StartZ=0 EndX=50.8 EndY=252.6 EndZ=0
    g2: LineSegment [constr] StartX=50.8 StartY=252.6 StartZ=0 EndX=-50.8 EndY=252.6 EndZ=0
    g3: LineSegment [constr] StartX=-50.8 StartY=252.6 StartZ=0 EndX=-50.8 EndY=24 EndZ=0
    g4: LineSegment StartX=-54.8 StartY=256.6 StartZ=0 EndX=-54.8 EndY=20 EndZ=0
    g5: LineSegment [constr] StartX=-54.8 StartY=20 StartZ=0 EndX=54.8 EndY=20 EndZ=0
    g6: LineSegment StartX=34.8 StartY=162.959 StartZ=0 EndX=-34.8 EndY=162.959 EndZ=0
    g7: LineSegment StartX=-34.8 StartY=162.959 StartZ=0 EndX=-34.8 EndY=149.512 EndZ=0
    g8: LineSegment StartX=-34.8 StartY=149.512 StartZ=0 EndX=34.8 EndY=149.512 EndZ=0
    g9: LineSegment StartX=34.8 StartY=149.512 StartZ=0 EndX=34.8 EndY=162.959 EndZ=0
    g10: LineSegment StartX=34.8 StartY=107.062 StartZ=0 EndX=-34.8 EndY=107.062 EndZ=0
    g11: LineSegment StartX=-34.8 StartY=107.062 StartZ=0 EndX=-34.8 EndY=134.512 EndZ=0
    g12: LineSegment StartX=-34.8 StartY=134.512 StartZ=0 EndX=34.8 EndY=134.512 EndZ=0
    g13: LineSegment StartX=34.8 StartY=134.512 StartZ=0 EndX=34.8 EndY=107.062 EndZ=0
    g14: LineSegment StartX=34.8 StartY=239 StartZ=0 EndX=-34.8 EndY=239 EndZ=0
    g15: LineSegment StartX=-34.8 StartY=239 StartZ=0 EndX=-34.8 EndY=220.485 EndZ=0
    g16: LineSegment StartX=-34.8 StartY=220.485 StartZ=0 EndX=34.8 EndY=220.485 EndZ=0
    g17: LineSegment StartX=34.8 StartY=220.485 StartZ=0 EndX=34.8 EndY=239 EndZ=0
    g18: LineSegment StartX=34.8 StartY=182.959 StartZ=0 EndX=-34.8 EndY=182.959 EndZ=0
    g19: LineSegment StartX=-34.8 StartY=182.959 StartZ=0 EndX=-34.8 EndY=205.485 EndZ=0
    g20: LineSegment StartX=-34.8 StartY=205.485 StartZ=0 EndX=34.8 EndY=205.485 EndZ=0
    g21: LineSegment StartX=34.8 StartY=205.485 StartZ=0 EndX=34.8 EndY=182.959 EndZ=0
    g22: LineSegment StartX=-34.8 StartY=81.9803 StartZ=0 EndX=-34.8 EndY=59.2632 EndZ=0
    g23: LineSegment StartX=-34.8 StartY=59.2632 StartZ=0 EndX=34.8 EndY=59.2632 EndZ=0
    g24: LineSegment StartX=34.8 StartY=59.2632 StartZ=0 EndX=34.8 EndY=81.9803 EndZ=0
    g25: LineSegment StartX=34.8 StartY=81.9803 StartZ=0 EndX=-34.8 EndY=81.9803 EndZ=0
    g26: LineSegment StartX=-34.8 StartY=44.2632 StartZ=0 EndX=-34.8 EndY=15 EndZ=0
    g27: LineSegment StartX=-34.8 StartY=15 StartZ=0 EndX=34.8 EndY=15 EndZ=0
    g28: LineSegment StartX=34.8 StartY=15 StartZ=0 EndX=34.8 EndY=44.2632 EndZ=0
    g29: LineSegment StartX=34.8 StartY=44.2632 StartZ=0 EndX=-34.8 EndY=44.2632 EndZ=0
    g30: LineSegment StartX=54.8 StartY=20 StartZ=0 EndX=54.8 EndY=256.6 EndZ=0
    g31: LineSegment [constr] StartX=-54.8 StartY=256.6 StartZ=0 EndX=54.8 EndY=256.6 EndZ=0
    g32: LineSegment StartX=-54.8 StartY=20 StartZ=0 EndX=-54.8 EndY=0 EndZ=0
    g33: LineSegment StartX=-54.8 StartY=0 StartZ=0 EndX=54.8 EndY=0 EndZ=0
    g34: LineSegment StartX=54.8 StartY=0 StartZ=0 EndX=54.8 EndY=20 EndZ=0
    g35: LineSegment [constr] StartX=54.8 StartY=20 StartZ=0 EndX=-54.8 EndY=20 EndZ=0
    g36: LineSegment StartX=-54.8 StartY=256.6 StartZ=0 EndX=-54.8 EndY=259 EndZ=0
    g37: LineSegment StartX=-54.8 StartY=259 StartZ=0 EndX=54.8 EndY=259 EndZ=0
    g38: LineSegment StartX=54.8 StartY=259 StartZ=0 EndX=54.8 EndY=256.6 EndZ=0
    g39: Circle CenterX=-44.8 CenterY=30 CenterZ=0 NormalX=0 NormalY=0 NormalZ=1 AngleXU=0 Radius=0.855
    g40: Circle CenterX=44.8 CenterY=30 CenterZ=0 NormalX=0 NormalY=0 NormalZ=1 AngleXU=0 Radius=0.855
    g41: Circle CenterX=-44.8 CenterY=125 CenterZ=0 NormalX=0 NormalY=0 NormalZ=1 AngleXU=0 Radius=0.855
    g42: Circle CenterX=44.8 CenterY=125 CenterZ=0 NormalX=0 NormalY=0 NormalZ=1 AngleXU=0 Radius=0.855
    g43: Circle CenterX=-44.8 CenterY=170 CenterZ=0 NormalX=0 NormalY=0 NormalZ=1 AngleXU=0 Radius=0.855
    g44: Circle CenterX=44.8 CenterY=170 CenterZ=0 NormalX=0 NormalY=0 NormalZ=1 AngleXU=0 Radius=0.855
    g45: Circle CenterX=-44.8 CenterY=145 CenterZ=0 NormalX=0 NormalY=0 NormalZ=1 AngleXU=0 Radius=0.855
    g46: Circle CenterX=44.8 CenterY=145 CenterZ=0 NormalX=0 NormalY=0 NormalZ=1 AngleXU=0 Radius=0.855
    g47: Circle CenterX=-44.8 CenterY=230 CenterZ=0 NormalX=0 NormalY=0 NormalZ=1 AngleXU=0 Radius=0.855
    g48: Circle CenterX=44.8 CenterY=230 CenterZ=0 NormalX=0 NormalY=0 NormalZ=1 AngleXU=0 Radius=0.855
    g49: LineSegment StartX=-34.8 StartY=89.607 StartZ=0 EndX=34.8 EndY=89.607 EndZ=0
    g50: LineSegment StartX=34.8 StartY=89.607 StartZ=0 EndX=34.8 EndY=98.0817 EndZ=0
    g51: LineSegment StartX=34.8 StartY=98.0817 StartZ=0 EndX=-34.8 EndY=98.0817 EndZ=0
    g52: LineSegment StartX=-34.8 StartY=98.0817 StartZ=0 EndX=-34.8 EndY=89.607 EndZ=0
    g53: Circle CenterX=-44.8 CenterY=104 CenterZ=0 NormalX=0 NormalY=0 NormalZ=1 AngleXU=0 Radius=0.855
    g54: Circle CenterX=44.8 CenterY=104 CenterZ=0 NormalX=0 NormalY=0 NormalZ=1 AngleXU=0 Radius=0.85
  constraints (151):
    c: Coincident(g0,g1)
    c: Coincident(g1,g2)
    c: Coincident(g2,g3)
    c: Coincident(g3,g0)
    c: Horizontal(g2)
    c: Vertical(g1)
    c: Vertical(g3)
    c: DistanceY(g0,g2) = 228.6
    c: DistanceX(g0,g0) = 101.6
    c: DistanceX(g0,g-1) = 50.8
    c: Coincident(g4,g5)
    c: Vertical(g4)
    c: Horizontal(g5)
    c: DistanceX(g4,g0) = 4
    c: Horizontal(g0)
    c: Coincident(g6,g7)
    c: Coincident(g7,g8)
    c: Coincident(g8,g9)
    c: Coincident(g9,g6)
    c: Horizontal(g6)
    c: Horizontal(g8)
    c: Vertical(g7)
    c: Vertical(g9)
    c: Coincident(g10,g11)
    c: Coincident(g11,g12)
    c: Coincident(g12,g13)
    c: Coincident(g13,g10)
    c: Horizontal(g10)
    c: Horizontal(g12)
    c: Vertical(g11)
    c: Vertical(g13)
    c: Coincident(g14,g15)
    c: Coincident(g15,g16)
    c: Coincident(g16,g17)
    c: Coincident(g17,g14)
    c: Horizontal(g14)
    c: Horizontal(g16)
    c: Vertical(g15)
    c: Vertical(g17)
    c: Coincident(g18,g19)
    c: Coincident(g19,g20)
    c: Coincident(g20,g21)
    c: Coincident(g21,g18)
    c: Horizontal(g18)
    c: Horizontal(g20)
    c: Vertical(g19)
    c: DistanceY(g20,g16) = 15
    c: Vertical(g12,g18)
    c: DistanceY(g6,g18) = 20
    c: Coincident(g22,g23)
    c: Coincident(g23,g24)
    c: Coincident(g24,g25)
    c: Coincident(g25,g22)
    c: Vertical(g22)
    c: Vertical(g24)
    c: Horizontal(g23)
    c: Horizontal(g25)
    c: Coincident(g26,g27)
    c: Coincident(g27,g28)
    c: Coincident(g28,g29)
    c: Coincident(g29,g26)
    c: Vertical(g26)
    c: Vertical(g28)
    c: Horizontal(g27)
    c: Horizontal(g29)
    c: DistanceY(g26,g22) = 15
    c: Vertical(g22,g26)
    c: Vertical(g10,g24)
    c: Vertical(g24,g28)
    c: Coincident(g30,g5)
    c: Vertical(g30)
    c: DistanceY(g1,g30) = 4
    c: Horizontal(g4,g30)
    c: Coincident(g31,g4)
    c: Coincident(g31,g30)
    c: DistanceX(g4,g5) = 109.6
    c: DistanceY(g-1,g5) = 20
    c: Coincident(g32,g33)
    c: Coincident(g33,g34)
    c: Coincident(g34,g35)
    c: Coincident(g35,g32)
    c: Vertical(g32)
    c: Vertical(g34)
    c: Horizontal(g33)
    c: Horizontal(g35)
    c: Coincident(g32,g4)
    c: Horizontal(g33,g-1)
    c: Vertical(g34,g5)
    c: Vertical(g21)
    c: Coincident(g36,g4)
    c: Vertical(g36)
    c: Coincident(g37,g36)
    c: Horizontal(g37)
    c: Coincident(g38,g37)
    c: Coincident(g38,g30)
    c: Vertical(g38)
    c: DistanceY(g-1,g26) = 15
    c: DistanceX(g32,g26) = 20
    c: DistanceX(g27,g33) = 20
    c: Vertical(g10,g22)
    c: Vertical(g11,g7)
    c: Vertical(g6,g18)
    c: Vertical(g19,g15)
    c: Vertical(g12,g8)
    c: Vertical(g20,g16)
    c: DistanceY(g12,g8) = 15
    c: DistanceY(g33,g37) = 259
    c: Diameter(g39) = 1.71
    c: Diameter(g40) = 1.71
    c: Horizontal(g40,g39)
    c: DistanceX(g4,g39) = 10
    c: DistanceX(g40,g5) = 10
    c: Diameter(g41) = 1.71
    c: Diameter(g42) = 1.71
    c: Horizontal(g42,g41)
    c: Diameter(g43) = 1.71
    c: Diameter(g44) = 1.71
    c: Horizontal(g44,g43)
    c: Vertical(g43,g39)
    c: Vertical(g44,g42)
    c: Diameter(g45) = 1.71
    c: Diameter(g46) = 1.71
    c: Horizontal(g46,g45)
    c: DistanceY(g-1,g39) = 30
    c: DistanceY(g-1,g41) = 125
    c: Vertical(g45,g41)
    c: DistanceY(g-1,g45) = 145
    c: DistanceY(g-1,g43) = 170
    c: Vertical(g42,g46)
    c: Diameter(g48) = 1.71
    c: Diameter(g47) = 1.71
    c: Vertical(g48,g44)
    c: Vertical(g47,g43)
    c: DistanceY(g-1,g47) = 230
    c: Horizontal(g48,g47)
    c: Coincident(g49,g50)
    c: Coincident(g50,g51)
    c: Coincident(g51,g52)
    c: Coincident(g52,g49)
    c: Horizontal(g49)
    c: Horizontal(g51)
    c: Vertical(g50)
    c: Vertical(g52)
    c: Vertical(g49,g22)
    c: Vertical(g49,g24)
    c: Diameter(g53) = 1.71
    c: Vertical(g41,g53)
    c: Diameter(g54) = 1.7
    c: Horizontal(g53,g54)
    c: Vertical(g54,g42)
    c: DistanceY(g-1,g53) = 104
FEATURE [PartDesign::Pad] Pad004  label="Frontplate Pad"
  Direction = (0,-1,2e-16)
  Length = 3
  Length2 = 10
  Placement = pos=(0,0,0) rot=(1,0,0;1.5708rad)
  Profile = -> Sketch005
  ReferenceAxis = -> Sketch005 [N_Axis]
  Reversed = true
  Suppressed = false
  Type = 0
  expr: Length = <<Monitor Chassis Parameters>>.GSBackPlateThickness
FEATURE [Sketcher::SketchObject] Sketch007  label="Frontplate Foot Sketch"
  ArcFitTolerance = 1e-06
  AttachmentSupport = -> [XZ_Plane002]
  FullyConstrained = true
  MakeInternals = false
  MapMode = 5
  Placement = pos=(0,0,0) rot=(1,0,0;1.5708rad)
  expr: Constraints[11] = <<Monitor Chassis Parameters>>.GSTowerFeetThickness
  expr: Constraints[21] = <<Monitor Chassis Parameters>>.GSTowerFeetThickness
  expr: Constraints[22] = <<Monitor Chassis Parameters>>.GSBackPlateFootWidth
  expr: Constraints[23] = 0.5 * <<Monitor Chassis Parameters>>.GSBackPlateWidth
  expr: Constraints[8] = <<Monitor Chassis Parameters>>.GSBackPlateFootWidth
  expr: Constraints[9] = 0.5 * <<Monitor Chassis Parameters>>.GSBackPlateWidth
  sketch-geometry (8):
    g0: LineSegment StartX=-54.8 StartY=-5 StartZ=0 EndX=-19.8 EndY=-5 EndZ=0
    g1: LineSegment StartX=-19.8 StartY=-5 StartZ=0 EndX=-19.8 EndY=0 EndZ=0
    g2: LineSegment StartX=-19.8 StartY=0 StartZ=0 EndX=-54.8 EndY=0 EndZ=0
    g3: LineSegment StartX=-54.8 StartY=0 StartZ=0 EndX=-54.8 EndY=-5 EndZ=0
    g4: LineSegment StartX=54.8 StartY=-5 StartZ=0 EndX=54.8 EndY=0 EndZ=0
    g5: LineSegment StartX=54.8 StartY=0 StartZ=0 EndX=19.8 EndY=0 EndZ=0
    g6: LineSegment StartX=19.8 StartY=0 StartZ=0 EndX=19.8 EndY=-5 EndZ=0
    g7: LineSegment StartX=19.8 StartY=-5 StartZ=0 EndX=54.8 EndY=-5 EndZ=0
  constraints (24):
    c: Coincident(g0,g1)
    c: Coincident(g1,g2)
    c: Coincident(g2,g3)
    c: Coincident(g3,g0)
    c: Horizontal(g0)
    c: Horizontal(g2)
    c: Vertical(g1)
    c: Vertical(g3)
    c: DistanceX(g2,g1) = 35
    c: DistanceX(g2,g-1) = 54.8
    c: Horizontal(g2,g-1)
    c: DistanceY(g0,g2) = 5
    c: Coincident(g4,g5)
    c: Coincident(g5,g6)
    c: Coincident(g6,g7)
    c: Coincident(g7,g4)
    c: Vertical(g4)
    c: Vertical(g6)
    c: Horizontal(g5)
    c: Horizontal(g7)
    c: Horizontal(g5,g-1)
    c: DistanceY(g4,g4) = 5
    c: DistanceX(g6,g4) = 35
    c: DistanceX(g-1,g4) = 54.8
FEATURE [PartDesign::Pad] Pad006  label="Frontplate Foot Pad"
  BaseFeature = -> Pad004
  Direction = (0,-1,2e-16)
  Length = 65
  Length2 = 3
  Placement = pos=(0,0,0) rot=(1,0,0;1.5708rad)
  Profile = -> Sketch007
  ReferenceAxis = -> Sketch007 [N_Axis]
  Suppressed = false
  Type = 4
  expr: Length = <<Monitor Chassis Parameters>>.GSBackPlateFootLengthForward
  expr: Length2 = <<Monitor Chassis Parameters>>.GSBackPlateThickness
FEATURE [Sketcher::SketchObject] Sketch008  label="Frontplate Foot Screw Holes Sketch"
  ArcFitTolerance = 1e-06
  AttachmentSupport = -> [XY_Plane002]
  FullyConstrained = true
  MakeInternals = false
  MapMode = 5
  expr: Constraints[0] = <<Monitor Chassis Parameters>>.GSBackPlateFootScrewHoleForwardOffset
  expr: Constraints[1] = 0.5 * <<Monitor Chassis Parameters>>.GSBackPlateWidth - 0.5 * <<Monitor Chassis Parameters>>.GSBackPlateFootWidth
  expr: Constraints[2] = 0.5 * <<Monitor Chassis Parameters>>.GSBackPlateWidth - 0.5 * <<Monitor Chassis Parameters>>.GSBackPlateFootWidth
  expr: Constraints[3] = <<Monitor Chassis Parameters>>.GSTowerFeetScrewDiameter
  expr: Constraints[4] = <<Monitor Chassis Parameters>>.GSTowerFeetScrewDiameter
  sketch-geometry (2):
    g0: Circle CenterX=-37.3 CenterY=-59 CenterZ=0 NormalX=0 NormalY=0 NormalZ=1 AngleXU=0 Radius=1.7
    g1: Circle CenterX=37.3 CenterY=-59 CenterZ=0 NormalX=0 NormalY=0 NormalZ=1 AngleXU=0 Radius=1.7
  constraints (6):
    c: DistanceY(g0,g-1) = 59
    c: DistanceX(g0,g-1) = 37.3
    c: DistanceX(g-1,g1) = 37.3
    c: Diameter(g0) = 3.4
    c: Diameter(g1) = 3.4
    c: Horizontal(g1,g0)
FEATURE [PartDesign::Hole] Hole001  label="Frontplate Foot Screw Holes"
  BaseFeature = -> Pad006
  CustomThreadClearance = 0
  Depth = 25
  DepthType = 0
  Diameter = 3.4
  DrillForDepth = false
  DrillPoint = 1
  DrillPointAngle = 118
  HoleCutCountersinkAngle = 90
  HoleCutCustomValues = false
  HoleCutDepth = 0
  HoleCutDiameter = 8
  HoleCutType = 2
  ModelThread = false
  Placement = pos=(0,0,0) rot=(1,0,0;1.5708rad)
  Profile = -> Sketch008
  Suppressed = false
  Tapered = false
  TaperedAngle = 90
  ThreadClass = 0
  ThreadDepth = 25
  ThreadDepthType = 0
  ThreadDirection = 0
  ThreadFit = 0
  ThreadSize = 0
  ThreadType = 0
  Threaded = false
  UseCustomThreadClearance = false
  expr: Diameter = <<Monitor Chassis Parameters>>.GSTowerFeetScrewDiameter
  expr: HoleCutDiameter = <<Monitor Chassis Parameters>>.GSM4BoltCountersinkDiameter
FEATURE [Sketcher::SketchObject] Sketch009  label="Frontplate Foot Support Corner Sketch"
  ArcFitTolerance = 1e-06
  AttachmentSupport = -> [DatumPlane001]
  FullyConstrained = true
  MakeInternals = false
  MapMode = 5
  Placement = pos=(54.8,0,0) rot=(0.57735,0.57735,0.57735;2.0944rad)
  expr: Constraints[1] = <<Monitor Chassis Parameters>>.GSBackPlateThickness
  expr: Constraints[24] = 0.8 * <<Monitor Chassis Parameters>>.GSTowerFloorDepth
  expr: Constraints[25] = 0.6 * <<Monitor Chassis Parameters>>.GSTowerFloorDepth
  expr: Constraints[26] = <<Monitor Chassis Parameters>>.GSSideCornerCutoutInset
  expr: Constraints[27] = <<Monitor Chassis Parameters>>.GSSideCornerCutoutInset
  expr: Constraints[28] = 2 * <<Monitor Chassis Parameters>>.GSSideCornerCutoutInset
  expr: Constraints[29] = 3 * <<Monitor Chassis Parameters>>.GSSideCornerCutoutInset
  expr: Constraints[39] = 0.8 * <<Monitor Chassis Parameters>>.GSTowerFloorDepth
  expr: Constraints[3] = <<Monitor Chassis Parameters>>.GSTowerFeetThickness
  expr: Constraints[41] = <<Monitor Chassis Parameters>>.GSSideCornerCutoutInset
  expr: Constraints[42] = -2 * <<Monitor Chassis Parameters>>.GSSideCornerCutoutInset
  expr: Constraints[43] = 3 * <<Monitor Chassis Parameters>>.GSSideCornerCutoutInset
  expr: Constraints[54] = 0.8 * <<Monitor Chassis Parameters>>.GSTowerFloorDepth
  expr: Constraints[55] = 0.6 * <<Monitor Chassis Parameters>>.GSTowerFloorDepth
  expr: Constraints[56] = <<Monitor Chassis Parameters>>.GSSideCornerCutoutInset
  expr: Constraints[57] = <<Monitor Chassis Parameters>>.GSSideCornerCutoutInset
  expr: Constraints[58] = 2 * <<Monitor Chassis Parameters>>.GSSideCornerCutoutInset
  expr: Constraints[59] = 3 * <<Monitor Chassis Parameters>>.GSSideCornerCutoutInset
  expr: Constraints[62] = <<Monitor Chassis Parameters>>.GSTowerThirdFloorHeight
  expr: Constraints[63] = <<Monitor Chassis Parameters>>.GSTowerSecondFloorHeight
  expr: Constraints[64] = 0.6 * <<Monitor Chassis Parameters>>.GSTowerFloorDepth
  expr: Constraints[65] = <<Monitor Chassis Parameters>>.GSTowerFourthFloorHeight + <<Monitor Chassis Parameters>>.GSTowerFloorThickness
  expr: Constraints[6] = 0.8 * <<Monitor Chassis Parameters>>.GSTowerFloorDepth
  expr: Constraints[70] = 2 * <<Monitor Chassis Parameters>>.GSSideCornerCutoutInset
  expr: Constraints[71] = 3 * <<Monitor Chassis Parameters>>.GSSideCornerCutoutInset
  expr: Constraints[73] = <<Monitor Chassis Parameters>>.GSSideCornerCutoutInset
  expr: Constraints[7] = 0.6 * <<Monitor Chassis Parameters>>.GSTowerFloorDepth
  sketch-geometry (24):
    g0: LineSegment StartX=-41 StartY=-5 StartZ=0 EndX=3 EndY=-5 EndZ=0
    g1: LineSegment StartX=3 StartY=28 StartZ=0 EndX=3 EndY=-5 EndZ=0
    g2: LineSegment StartX=-41 StartY=-5 StartZ=0 EndX=3 EndY=28 EndZ=0
    g3: LineSegment StartX=-23 StartY=181 StartZ=0 EndX=-3 EndY=196 EndZ=0
    g4: LineSegment StartX=-3 StartY=196 StartZ=0 EndX=-3 EndY=181 EndZ=0
    g5: LineSegment StartX=-23 StartY=181 StartZ=0 EndX=-3 EndY=181 EndZ=0
    g6: LineSegment StartX=3 StartY=208 StartZ=0 EndX=3 EndY=175 EndZ=0
    g7: LineSegment StartX=3 StartY=175 StartZ=0 EndX=-41 EndY=175 EndZ=0
    g8: LineSegment StartX=-41 StartY=175 StartZ=0 EndX=3 EndY=208 EndZ=0
    g9: LineSegment StartX=-23 StartY=1 StartZ=0 EndX=-3 EndY=16 EndZ=0
    g10: LineSegment StartX=-3 StartY=16 StartZ=0 EndX=-3 EndY=1 EndZ=0
    g11: LineSegment StartX=-23 StartY=1 StartZ=0 EndX=-3 EndY=1 EndZ=0
    g12: LineSegment StartX=-23 StartY=253 StartZ=0 EndX=-3 EndY=238 EndZ=0
    g13: LineSegment StartX=-3 StartY=238 StartZ=0 EndX=-3 EndY=253 EndZ=0
    g14: LineSegment StartX=-23 StartY=253 StartZ=0 EndX=-3 EndY=253 EndZ=0
    g15: LineSegment StartX=3 StartY=226 StartZ=0 EndX=3 EndY=259 EndZ=0
    g16: LineSegment StartX=3 StartY=259 StartZ=0 EndX=-41 EndY=259 EndZ=0
    g17: LineSegment StartX=-41 StartY=259 StartZ=0 EndX=3 EndY=226 EndZ=0
    g18: LineSegment StartX=-23 StartY=91 StartZ=0 EndX=-3 EndY=106 EndZ=0
    g19: LineSegment StartX=-3 StartY=106 StartZ=0 EndX=-3 EndY=91 EndZ=0
    g20: LineSegment StartX=-23 StartY=91 StartZ=0 EndX=-3 EndY=91 EndZ=0
    g21: LineSegment StartX=3 StartY=118 StartZ=0 EndX=3 EndY=85 EndZ=0
    g22: LineSegment StartX=3 StartY=85 StartZ=0 EndX=-41 EndY=85 EndZ=0
    g23: LineSegment StartX=-41 StartY=85 StartZ=0 EndX=3 EndY=118 EndZ=0
  constraints (74):
    c: Horizontal(g0)
    c: DistanceX(g-1,g0) = 3
    c: Vertical(g1)
    c: DistanceY(g0,g-1) = 5
    c: Coincident(g2,g0)
    c: Coincident(g2,g1)
    c: DistanceX(g0,g0) = 44
    c: DistanceY(g0,g1) = 33
    c: Coincident(g4,g3)
    c: Vertical(g4)
    c: Coincident(g5,g3)
    c: Coincident(g5,g4)
    c: Horizontal(g5)
    c: Vertical(g6)
    c: Coincident(g7,g6)
    c: Horizontal(g7)
    c: Coincident(g8,g7)
    c: Coincident(g8,g6)
    c: Coincident(g10,g9)
    c: Vertical(g10)
    c: Coincident(g11,g9)
    c: Coincident(g11,g10)
    c: Horizontal(g11)
    c: Vertical(g6,g1)
    c: DistanceX(g7,g6) = 44
    c: DistanceY(g6,g6) = 33
    c: DistanceY(g6,g4) = 6
    c: DistanceX(g4,g6) = 6
    c: DistanceY(g3,g6) = 12
    c: DistanceX(g7,g3) = 18
    c: Coincident(g13,g12)
    c: Vertical(g13)
    c: Coincident(g14,g12)
    c: Coincident(g14,g13)
    c: Horizontal(g14)
    c: Vertical(g15)
    c: Horizontal(g16)
    c: Coincident(g17,g16)
    c: Coincident(g17,g15)
    c: DistanceX(g16,g15) = 44
    c: DistanceY(g15,g13) = -6
    c: DistanceX(g13,g15) = 6
    c: DistanceY(g12,g15) = -12
    c: DistanceX(g16,g12) = 18
    c: Coincident(g19,g18)
    c: Vertical(g19)
    c: Coincident(g20,g18)
    c: Coincident(g20,g19)
    c: Horizontal(g20)
    c: Vertical(g21)
    c: Coincident(g22,g21)
    c: Horizontal(g22)
    c: Coincident(g23,g22)
    c: Coincident(g23,g21)
    c: DistanceX(g22,g21) = 44
    c: DistanceY(g21,g21) = 33
    c: DistanceY(g21,g19) = 6
    c: DistanceX(g19,g21) = 6
    c: DistanceY(g18,g21) = 12
    c: DistanceX(g22,g18) = 18
    c: Vertical(g21,g6)
    c: Vertical(g6,g15)
    c: DistanceY(g-1,g6) = 175
    c: DistanceY(g-1,g21) = 85
    c: DistanceY(g15,g15) = 33
    c: DistanceY(g-1,g15) = 259
    c: Horizontal(g16,g15)
    c: Vertical(g16,g15)
    c: Vertical(g1,g0)
    c: Horizontal(g1,g0)
    c: DistanceY(g9,g1) = 12
    c: DistanceX(g0,g9) = 18
    c: Vertical(g19,g9)
    c: DistanceY(g0,g10) = 6
FEATURE [PartDesign::Pad] Pad007  label="Frontplate Floor Support Corner Pad"
  BaseFeature = -> Hole001
  Direction = (1,0,0)
  Length = 2.5
  Length2 = 10
  Placement = pos=(0,0,0) rot=(1,0,0;1.5708rad)
  Profile = -> Sketch009
  ReferenceAxis = -> Sketch009 [N_Axis]
  Suppressed = false
  Type = 0
  expr: Length = <<Monitor Chassis Parameters>>.GSSideCornerThickness
FEATURE [PartDesign::Mirrored] Mirrored001  label="Frontplate Floor Support Corner Mirrored"
  BaseFeature = -> Pad007
  MirrorPlane = -> YZ_Plane002
  Originals = -> [Pad007]
  Placement = pos=(0,0,0) rot=(1,0,0;1.5708rad)
  Suppressed = false
  TransformMode = 0
FEATURE [Sketcher::SketchObject] Sketch010  label="Frontplate Floors Sketch"
  ArcFitTolerance = 1e-06
  AttachmentSupport = -> [DatumPlane001]
  FullyConstrained = true
  MakeInternals = false
  MapMode = 5
  Placement = pos=(54.8,0,0) rot=(0.57735,0.57735,0.57735;2.0944rad)
  expr: Constraints[10] = <<Monitor Chassis Parameters>>.GSTowerSecondFloorDepth
  expr: Constraints[21] = <<Monitor Chassis Parameters>>.GSTowerFourthFloorDepth
  expr: Constraints[32] = <<Monitor Chassis Parameters>>.GSTowerThirdFloorDepth
  expr: Constraints[43] = <<Monitor Chassis Parameters>>.GSTowerFirstFloorDepth
  expr: Constraints[44] = <<Monitor Chassis Parameters>>.GSTowerFirstFloorHeight
  expr: Constraints[45] = <<Monitor Chassis Parameters>>.GSTowerSecondFloorHeight
  expr: Constraints[46] = <<Monitor Chassis Parameters>>.GSTowerFourthFloorHeight
  expr: Constraints[47] = <<Monitor Chassis Parameters>>.GSTowerThirdFloorHeight
  expr: Constraints[9] = <<Monitor Chassis Parameters>>.GSTowerFloorThickness
  sketch-geometry (16):
    g0: LineSegment StartX=-55 StartY=85 StartZ=0 EndX=0 EndY=85 EndZ=0
    g1: LineSegment StartX=0 StartY=85 StartZ=0 EndX=0 EndY=89 EndZ=0
    g2: LineSegment StartX=0 StartY=89 StartZ=0 EndX=-55 EndY=89 EndZ=0
    g3: LineSegment StartX=-55 StartY=89 StartZ=0 EndX=-55 EndY=85 EndZ=0
    g4: LineSegment StartX=-55 StartY=255 StartZ=0 EndX=0 EndY=255 EndZ=0
    g5: LineSegment StartX=0 StartY=255 StartZ=0 EndX=0 EndY=259 EndZ=0
    g6: LineSegment StartX=0 StartY=259 StartZ=0 EndX=-55 EndY=259 EndZ=0
    g7: LineSegment StartX=-55 StartY=259 StartZ=0 EndX=-55 EndY=255 EndZ=0
    g8: LineSegment StartX=-55 StartY=175 StartZ=0 EndX=0 EndY=175 EndZ=0
    g9: LineSegment StartX=0 StartY=175 StartZ=0 EndX=0 EndY=179 EndZ=0
    g10: LineSegment StartX=0 StartY=179 StartZ=0 EndX=-55 EndY=179 EndZ=0
    g11: LineSegment StartX=-55 StartY=179 StartZ=0 EndX=-55 EndY=175 EndZ=0
    g12: LineSegment StartX=-50 StartY=5 StartZ=0 EndX=0 EndY=5 EndZ=0
    g13: LineSegment StartX=0 StartY=5 StartZ=0 EndX=0 EndY=9 EndZ=0
    g14: LineSegment StartX=0 StartY=9 StartZ=0 EndX=-50 EndY=9 EndZ=0
    g15: LineSegment StartX=-50 StartY=9 StartZ=0 EndX=-50 EndY=5 EndZ=0
  constraints (48):
    c: Coincident(g0,g1)
    c: Coincident(g1,g2)
    c: Coincident(g2,g3)
    c: Coincident(g3,g0)
    c: Horizontal(g0)
    c: Horizontal(g2)
    c: Vertical(g1)
    c: Vertical(g3)
    c: Vertical(g0,g-1)
    c: DistanceY(g0,g2) = 4
    c: DistanceX(g2,g1) = 55
    c: Coincident(g4,g5)
    c: Coincident(g5,g6)
    c: Coincident(g6,g7)
    c: Coincident(g7,g4)
    c: Horizontal(g4)
    c: Horizontal(g6)
    c: Vertical(g5)
    c: Vertical(g7)
    c: Vertical(g4,g-1)
    c: DistanceY(g4,g6) = 4
    c: DistanceX(g6,g5) = 55
    c: Coincident(g8,g9)
    c: Coincident(g9,g10)
    c: Coincident(g10,g11)
    c: Coincident(g11,g8)
    c: Horizontal(g8)
    c: Horizontal(g10)
    c: Vertical(g9)
    c: Vertical(g11)
    c: Vertical(g8,g-1)
    c: DistanceY(g8,g10) = 4
    c: DistanceX(g10,g9) = 55
    c: Coincident(g12,g13)
    c: Coincident(g13,g14)
    c: Coincident(g14,g15)
    c: Coincident(g15,g12)
    c: Horizontal(g12)
    c: Horizontal(g14)
    c: Vertical(g13)
    c: Vertical(g15)
    c: Vertical(g12,g-1)
    c: DistanceY(g12,g14) = 4
    c: DistanceX(g14,g13) = 50
    c: DistanceY(g-1,g12) = 5
    c: DistanceY(g-1,g0) = 85
    c: DistanceY(g-1,g4) = 255
    c: DistanceY(g-1,g8) = 175
FEATURE [PartDesign::Pad] Pad008  label="Tower Floors Pad"
  BaseFeature = -> Mirrored001
  Direction = (1,0,0)
  Length = 109.6
  Length2 = 10
  Placement = pos=(0,0,0) rot=(1,0,0;1.5708rad)
  Profile = -> Sketch010
  ReferenceAxis = -> Sketch010 [N_Axis]
  Reversed = true
  Suppressed = false
  Type = 0
  expr: Length = <<Monitor Chassis Parameters>>.GSBackPlateWidth
FEATURE [PartDesign::Plane] DatumPlane002  label="First Floor DatumPlane"
  AttachmentOffset = pos=(0,0,9) rot=(0,0,1;0rad)
  AttachmentSupport = -> [XY_Plane002]
  Length = 60
  MapMode = 5
  Placement = pos=(0,0,9) rot=(0,0,1;0rad)
  ResizeMode = 0
  Width = 60
  expr: .AttachmentOffset.Base.z = <<Monitor Chassis Parameters>>.GSTowerFirstFloorHeight + <<Monitor Chassis Parameters>>.GSTowerFloorThickness
FEATURE [PartDesign::Plane] DatumPlane003  label="Second Floor DatumPlane"
  AttachmentOffset = pos=(0,0,89) rot=(0,0,1;0rad)
  AttachmentSupport = -> [XY_Plane002]
  Length = 60
  MapMode = 5
  Placement = pos=(0,0,89) rot=(0,0,1;0rad)
  ResizeMode = 0
  Width = 60
  expr: .AttachmentOffset.Base.z = <<Monitor Chassis Parameters>>.GSTowerSecondFloorHeight + <<Monitor Chassis Parameters>>.GSTowerFloorThickness
FEATURE [PartDesign::Plane] DatumPlane004  label="Third Floor DatumPlane"
  AttachmentOffset = pos=(0,0,179) rot=(0,0,1;0rad)
  AttachmentSupport = -> [XY_Plane002]
  Length = 60
  MapMode = 5
  Placement = pos=(0,0,179) rot=(0,0,1;0rad)
  ResizeMode = 0
  Width = 60
  expr: .AttachmentOffset.Base.z = <<Monitor Chassis Parameters>>.GSTowerThirdFloorHeight + <<Monitor Chassis Parameters>>.GSTowerFloorThickness
FEATURE [Sketcher::SketchObject] Sketch011  label="Third Floor Holes Sketch"
  ArcFitTolerance = 1e-06
  AttachmentSupport = -> [DatumPlane004]
  FullyConstrained = true
  MakeInternals = false
  MapMode = 5
  Placement = pos=(0,0,179) rot=(0,0,1;0rad)
  expr: Constraints[1] = 2 + 0.5 * <<Monitor Chassis Parameters>>.GSTowerThirdFloorDepth
  expr: Constraints[2] = <<Monitor Chassis Parameters>>.GSMonitorFloorCameraMountHoleDiameter
  sketch-geometry (1):
    g0: Circle CenterX=0 CenterY=-29.5 CenterZ=0 NormalX=0 NormalY=0 NormalZ=1 AngleXU=0 Radius=2.75
  constraints (3):
    c: PointOnObject(g0,g-2)
    c: DistanceY(g0,g-1) = 29.5
    c: Diameter(g0) = 5.5
FEATURE [PartDesign::Pocket] Pocket  label="Third Floor Holes Pocket"
  BaseFeature = -> Pad008
  Direction = (0,0,-1)
  Length = 5
  Length2 = 5
  Placement = pos=(0,0,0) rot=(1,0,0;1.5708rad)
  Profile = -> Sketch011
  ReferenceAxis = -> Sketch011 [N_Axis]
  Suppressed = false
  Type = 0
FEATURE [Sketcher::SketchObject] Sketch012  label="Second Floor Holes Sketch"
  ArcFitTolerance = 1e-06
  AttachmentSupport = -> [DatumPlane003]
  FullyConstrained = true
  MakeInternals = false
  MapMode = 2
  Placement = pos=(0,0,89) rot=(0,0,1;0rad)
  expr: Constraints[0] = <<Monitor Chassis Parameters>>.GSMonitorFloorCameraMountHoleDiameter
  expr: Constraints[2] = 12 + 0.4 * <<Monitor Chassis Parameters>>.GSTowerSecondFloorDepth
  sketch-geometry (1):
    g0: Circle CenterX=0 CenterY=-34 CenterZ=0 NormalX=0 NormalY=0 NormalZ=1 AngleXU=0 Radius=2.75
  constraints (3):
    c: Diameter(g0) = 5.5
    c: Vertical(g-1,g0)
    c: DistanceY(g0,g-1) = 34
FEATURE [PartDesign::Pocket] Pocket001  label="Second Floor Holes Pocket"
  BaseFeature = -> Pocket
  Direction = (0,0,-1)
  Length = 5
  Length2 = 5
  Placement = pos=(0,0,0) rot=(1,0,0;1.5708rad)
  Profile = -> Sketch012
  ReferenceAxis = -> Sketch012 [N_Axis]
  Suppressed = false
  Type = 0
FEATURE [Sketcher::SketchObject] Sketch013  label="First Floor Holes Sketch"
  ArcFitTolerance = 1e-06
  AttachmentSupport = -> [DatumPlane002]
  FullyConstrained = true
  MakeInternals = false
  MapMode = 5
  Placement = pos=(0,0,9) rot=(0,0,1;0rad)
  expr: Constraints[0] = <<Monitor Chassis Parameters>>.GSMonitorFloorCameraMountHoleDiameter
  expr: Constraints[12] = <<Monitor Chassis Parameters>>.GSTowerFloorCameraPortWidth
  expr: Constraints[13] = <<Monitor Chassis Parameters>>.GSTowerFloorCameraPortLength
  expr: Constraints[14] = 0.5 * <<Monitor Chassis Parameters>>.GSTowerFloorCameraPortLength
  expr: Constraints[2] = 0.5 * <<Monitor Chassis Parameters>>.GSTowerFirstFloorDepth
  sketch-geometry (5):
    g0: Circle CenterX=0 CenterY=-25 CenterZ=0 NormalX=0 NormalY=0 NormalZ=1 AngleXU=0 Radius=2.75
    g1: LineSegment StartX=15 StartY=0 StartZ=0 EndX=-15 EndY=0 EndZ=0
    g2: LineSegment StartX=-15 StartY=0 StartZ=0 EndX=-15 EndY=-5 EndZ=0
    g3: LineSegment StartX=-15 StartY=-5 StartZ=0 EndX=15 EndY=-5 EndZ=0
    g4: LineSegment StartX=15 StartY=-5 StartZ=0 EndX=15 EndY=0 EndZ=0
  constraints (15):
    c: Diameter(g0) = 5.5
    c: Vertical(g0,g-1)
    c: DistanceY(g0,g-1) = 25
    c: Coincident(g1,g2)
    c: Coincident(g2,g3)
    c: Coincident(g3,g4)
    c: Coincident(g4,g1)
    c: Horizontal(g1)
    c: Horizontal(g3)
    c: Vertical(g2)
    c: Vertical(g4)
    c: PointOnObject(g1,g-1)
    c: DistanceY(g3,g1) = 5
    c: DistanceX(g2,g3) = 30
    c: DistanceX(g-1,g3) = 15
FEATURE [PartDesign::Pocket] Pocket002  label="First Floor Holes Pocket"
  BaseFeature = -> Pocket001
  Direction = (0,0,-1)
  Length = 5
  Length2 = 5
  Placement = pos=(0,0,0) rot=(1,0,0;1.5708rad)
  Profile = -> Sketch013
  ReferenceAxis = -> Sketch013 [N_Axis]
  Suppressed = false
  Type = 0
FEATURE [Sketcher::SketchObject] Sketch014  label="Shank Shield Riser Sketch"
  ArcFitTolerance = 1e-06
  AttachmentSupport = -> [XZ_Plane002]
  FullyConstrained = true
  MakeInternals = false
  MapMode = 5
  Placement = pos=(0,0,0) rot=(1,0,0;1.5708rad)
  expr: Constraints[0] = 3 * <<Monitor Chassis Parameters>>.GSM4TappingScrewHoleDiameter
  expr: Constraints[1] = <<Monitor Chassis Parameters>>.GSTowerFourthFloorHeight - 1.5 * <<Monitor Chassis Parameters>>.GSM4TappingScrewHoleDiameter
  expr: Constraints[2] = 0.5 * <<Monitor Chassis Parameters>>.GSBackPlateWidth - 1.5 * <<Monitor Chassis Parameters>>.GSM4TappingScrewHoleDiameter
  expr: Constraints[3] = 3 * <<Monitor Chassis Parameters>>.GSM4TappingScrewHoleDiameter
  expr: Constraints[5] = <<Monitor Chassis Parameters>>.GSBackPlateWidth - 3 * <<Monitor Chassis Parameters>>.GSM4TappingScrewHoleDiameter
  sketch-geometry (2):
    g0: Circle CenterX=-49.7 CenterY=249.9 CenterZ=0 NormalX=0 NormalY=0 NormalZ=1 AngleXU=0 Radius=5.1
    g1: Circle CenterX=49.7 CenterY=249.9 CenterZ=0 NormalX=0 NormalY=0 NormalZ=1 AngleXU=0 Radius=5.1
  constraints (6):
    c: Diameter(g0) = 10.2
    c: DistanceY(g-1,g0) = 249.9
    c: DistanceX(g0,g-1) = 49.7
    c: Diameter(g1) = 10.2
    c: Horizontal(g0,g1)
    c: DistanceX(g0,g1) = 99.4
FEATURE [PartDesign::Pad] Pad009  label="Shank Shield Riser Pad"
  BaseFeature = -> Pocket002
  Direction = (0,-1,2e-16)
  Length = 89.65
  Length2 = 10
  Placement = pos=(0,0,0) rot=(1,0,0;1.5708rad)
  Profile = -> Sketch014
  ReferenceAxis = -> Sketch014 [N_Axis]
  Suppressed = false
  Type = 0
  expr: Length = 1 + <<Monitor Chassis Parameters>>.GSBasePowerBoxTowerBackOffsetFromFront - <<Monitor Chassis Parameters>>.GSShankShieldThickness - <<Monitor Chassis Parameters>>.GSBackPlateThickness - 3 * <<Monitor Chassis Parameters>>.GSBasePowerBoxSideThickness
FEATURE [PartDesign::Plane] DatumPlane005  label="Shank Shield Riser Front DatumPlane005"
  AttachmentSupport = -> [Pad009]
  Length = 60
  MapMode = 5
  Placement = pos=(0,-89.65,0) rot=(1,0,0;1.5708rad)
  ResizeMode = 0
  Width = 60
FEATURE [Sketcher::SketchObject] Sketch015  label="Shank Shield Riser Screw Holes Sketch"
  ArcFitTolerance = 1e-06
  AttachmentSupport = -> [DatumPlane005]
  FullyConstrained = true
  MakeInternals = false
  MapMode = 5
  Placement = pos=(0,-89.65,0) rot=(1,0,0;1.5708rad)
  expr: Constraints[0] = 0.5 * <<Monitor Chassis Parameters>>.GSBackPlateWidth - 1.5 * <<Monitor Chassis Parameters>>.GSM4TappingScrewHoleDiameter
  expr: Constraints[1] = <<Monitor Chassis Parameters>>.GSM4TappingScrewHoleDiameter
  expr: Constraints[3] = <<Monitor Chassis Parameters>>.GSTowerFourthFloorHeight - 1.5 * <<Monitor Chassis Parameters>>.GSM4TappingScrewHoleDiameter
  expr: Constraints[4] = 0.5 * <<Monitor Chassis Parameters>>.GSBackPlateWidth - 1.5 * <<Monitor Chassis Parameters>>.GSM4TappingScrewHoleDiameter
  expr: Constraints[5] = <<Monitor Chassis Parameters>>.GSM4TappingScrewHoleDiameter
  sketch-geometry (2):
    g0: Circle CenterX=-49.7 CenterY=249.9 CenterZ=0 NormalX=0 NormalY=0 NormalZ=1 AngleXU=0 Radius=1.7
    g1: Circle CenterX=49.7 CenterY=249.9 CenterZ=0 NormalX=0 NormalY=0 NormalZ=1 AngleXU=0 Radius=1.7
  constraints (6):
    c: DistanceX(g0,g-1) = 49.7
    c: Diameter(g0) = 3.4
    c: Horizontal(g0,g1)
    c: DistanceY(g-1,g0) = 249.9
    c: DistanceX(g-1,g1) = 49.7
    c: Diameter(g1) = 3.4
FEATURE [PartDesign::Pocket] Pocket003  label="Shank Shield Riser Screw Holes Pocket"
  BaseFeature = -> Pad009
  Direction = (0,1,-2e-16)
  Length = 14
  Length2 = 5
  Placement = pos=(0,0,0) rot=(1,0,0;1.5708rad)
  Profile = -> Sketch015
  ReferenceAxis = -> Sketch015 [N_Axis]
  Suppressed = false
  Type = 0
  expr: Length = 14
FEATURE [PartDesign::Plane] DatumPlane006  label="Fourth Floor DatumPlane"
  AttachmentOffset = pos=(0,0,259) rot=(0,0,1;0rad)
  AttachmentSupport = -> [XY_Plane002]
  Length = 60
  MapMode = 5
  Placement = pos=(0,0,259) rot=(0,0,1;0rad)
  ResizeMode = 0
  Width = 60
  expr: .AttachmentOffset.Base.z = <<Monitor Chassis Parameters>>.GSTowerFourthFloorHeight + <<Monitor Chassis Parameters>>.GSTowerFloorThickness
FEATURE [Sketcher::SketchObject] Sketch016  label="Fourth Floor Cutout Sketch"
  ArcFitTolerance = 1e-06
  AttachmentSupport = -> [DatumPlane006]
  FullyConstrained = false
  MakeInternals = false
  MapMode = 5
  Placement = pos=(0,0,259) rot=(0,0,1;0rad)
  sketch-geometry (4):
    g0: LineSegment StartX=-44.9421 StartY=-8.20433 StartZ=0 EndX=-44.9421 EndY=-45.1974 EndZ=0
    g1: LineSegment StartX=-44.9421 StartY=-45.1974 StartZ=0 EndX=49.6477 EndY=-45.1974 EndZ=0
    g2: LineSegment StartX=49.6477 StartY=-45.1974 StartZ=0 EndX=49.6477 EndY=-8.20433 EndZ=0
    g3: LineSegment StartX=49.6477 StartY=-8.20433 StartZ=0 EndX=-44.9421 EndY=-8.20433 EndZ=0
  constraints (8):
    c: Coincident(g0,g1)
    c: Coincident(g1,g2)
    c: Coincident(g2,g3)
    c: Coincident(g3,g0)
    c: Vertical(g0)
    c: Vertical(g2)
    c: Horizontal(g1)
    c: Horizontal(g3)
FEATURE [PartDesign::Plane] DatumPlane007  label="Suggested Backplate Split DatumPlane"
  AttachmentOffset = pos=(0,0,102) rot=(0,0,1;0rad)
  AttachmentSupport = -> [XY_Plane001]
  Length = 60
  MapMode = 5
  Placement = pos=(0,0,102) rot=(0,0,1;0rad)
  ResizeMode = 0
  Width = 60
  expr: .AttachmentOffset.Base.z = 102
FEATURE [PartDesign::Plane] DatumPlane008  label="Suggested Frontplate Split DatumPlane"
  AttachmentOffset = pos=(0,0,145) rot=(0,0,1;0rad)
  AttachmentSupport = -> [XY_Plane002]
  Length = 60
  MapMode = 5
  Placement = pos=(0,0,145) rot=(0,0,1;0rad)
  ResizeMode = 0
  Width = 60
FEATURE [PartDesign::Body] Body001  label="Frontplate Body"
  AllowCompound = false
  Group = -> [Sketch005,Pad004,Sketch007,Pad006,Sketch008,Hole001,DatumPlane001,Sketch009,Pad007,Mirrored001,Sketch010,Pad008,DatumPlane002,DatumPlane003,DatumPlane004,Sketch011,Pocket,Sketch012,Pocket001,Sketch013,Pocket002,Sketch014,Pad009,DatumPlane005,Sketch015,Pocket003,DatumPlane006,Sketch016,DatumPlane008]
  Origin = -> Origin002
  Placement = pos=(0.1,5,0) rot=(0,0,1;3.14159rad)
  Tip = -> Pocket003
FEATURE [Sketcher::SketchObject] Sketch017  label="Tower Layer Join Screw Holes Sketch"
  ArcFitTolerance = 1e-06
  AttachmentSupport = -> [XZ_Plane001]
  FullyConstrained = true
  MakeInternals = false
  MapMode = 5
  Placement = pos=(0,0,0) rot=(1,0,0;1.5708rad)
  expr: Constraints[0] = <<Monitor Chassis Parameters>>.GSTowerLayerJoinScrewDiameter
  expr: Constraints[1] = <<Monitor Chassis Parameters>>.GSM2TappingScrewHoleDiameter
  expr: Constraints[22] = 0.5 * <<Monitor Chassis Parameters>>.GSBackPlateWidth - <<Monitor Chassis Parameters>>.GSTowerLayerJoinScrewInset
  expr: Constraints[23] = 0.5 * <<Monitor Chassis Parameters>>.GSBackPlateWidth - <<Monitor Chassis Parameters>>.GSTowerLayerJoinScrewInset
  expr: Constraints[24] = <<Monitor Chassis Parameters>>.GSTowerLayerJoinScrewHeightFromFoot_1
  expr: Constraints[25] = <<Monitor Chassis Parameters>>.GSTowerLayerJoinScrewHeightFromFoot_2
  expr: Constraints[26] = <<Monitor Chassis Parameters>>.GSTowerLayerJoinScrewHeightFromFoot_3
  expr: Constraints[27] = <<Monitor Chassis Parameters>>.GSTowerLayerJoinScrewHeightFromFoot_4
  expr: Constraints[28] = <<Monitor Chassis Parameters>>.GSTowerLayerJoinScrewHeightFromFoot_5
  expr: Constraints[29] = <<Monitor Chassis Parameters>>.GSM2TappingScrewHoleDiameter
  expr: Constraints[2] = <<Monitor Chassis Parameters>>.GSM2TappingScrewHoleDiameter
  expr: Constraints[30] = <<Monitor Chassis Parameters>>.GSM2TappingScrewHoleDiameter
  expr: Constraints[35] = <<Monitor Chassis Parameters>>.GSTowerLayerJoinScrewHeightFromFoot_6
  expr: Constraints[3] = <<Monitor Chassis Parameters>>.GSM2TappingScrewHoleDiameter
  expr: Constraints[4] = <<Monitor Chassis Parameters>>.GSM2TappingScrewHoleDiameter
  expr: Constraints[5] = <<Monitor Chassis Parameters>>.GSM2TappingScrewHoleDiameter
  expr: Constraints[6] = <<Monitor Chassis Parameters>>.GSM2TappingScrewHoleDiameter
  expr: Constraints[7] = <<Monitor Chassis Parameters>>.GSM2TappingScrewHoleDiameter
  expr: Constraints[8] = <<Monitor Chassis Parameters>>.GSM2TappingScrewHoleDiameter
  expr: Constraints[9] = <<Monitor Chassis Parameters>>.GSM2TappingScrewHoleDiameter
  sketch-geometry (12):
    g0: Circle CenterX=44.8 CenterY=170 CenterZ=0 NormalX=0 NormalY=0 NormalZ=1 AngleXU=0 Radius=0.855
    g1: Circle CenterX=-44.8 CenterY=145 CenterZ=0 NormalX=0 NormalY=0 NormalZ=1 AngleXU=0 Radius=0.855
    g2: Circle CenterX=44.8 CenterY=145 CenterZ=0 NormalX=0 NormalY=0 NormalZ=1 AngleXU=0 Radius=0.855
    g3: Circle CenterX=-44.8 CenterY=125 CenterZ=0 NormalX=0 NormalY=0 NormalZ=1 AngleXU=0 Radius=0.855
    g4: Circle CenterX=-44.8 CenterY=104 CenterZ=0 NormalX=0 NormalY=0 NormalZ=1 AngleXU=0 Radius=0.855
    g5: Circle CenterX=44.8 CenterY=125 CenterZ=0 NormalX=0 NormalY=0 NormalZ=1 AngleXU=0 Radius=0.855
    g6: Circle CenterX=44.8 CenterY=104 CenterZ=0 NormalX=0 NormalY=0 NormalZ=1 AngleXU=0 Radius=0.855
    g7: Circle CenterX=-44.8 CenterY=30 CenterZ=0 NormalX=0 NormalY=0 NormalZ=1 AngleXU=0 Radius=0.855
    g8: Circle CenterX=44.8 CenterY=30 CenterZ=0 NormalX=0 NormalY=0 NormalZ=1 AngleXU=0 Radius=0.855
    g9: Circle CenterX=-44.8 CenterY=170 CenterZ=0 NormalX=0 NormalY=0 NormalZ=1 AngleXU=0 Radius=0.855
    g10: Circle CenterX=-44.8 CenterY=230 CenterZ=0 NormalX=0 NormalY=0 NormalZ=1 AngleXU=0 Radius=0.855
    g11: Circle CenterX=44.8 CenterY=230 CenterZ=0 NormalX=0 NormalY=0 NormalZ=1 AngleXU=0 Radius=0.855
  constraints (36):
    c: Diameter(g0) = 1.71
    c: Diameter(g1) = 1.71
    c: Diameter(g2) = 1.71
    c: Diameter(g3) = 1.71
    c: Diameter(g4) = 1.71
    c: Diameter(g5) = 1.71
    c: Diameter(g6) = 1.71
    c: Diameter(g7) = 1.71
    c: Diameter(g8) = 1.71
    c: Diameter(g9) = 1.71
    c: Vertical(g9,g1)
    c: Vertical(g1,g3)
    c: Vertical(g4,g3)
    c: Vertical(g7,g4)
    c: Vertical(g8,g6)
    c: Vertical(g6,g5)
    c: Vertical(g5,g2)
    c: Vertical(g0,g2)
    c: Horizontal(g2,g1)
    c: Horizontal(g3,g5)
    c: Horizontal(g4,g6)
    c: Horizontal(g7,g8)
    c: DistanceX(g7,g-1) = 44.8
    c: DistanceX(g-1,g8) = 44.8
    c: DistanceY(g-1,g7) = 30
    c: DistanceY(g-1,g4) = 104
    c: DistanceY(g-1,g3) = 125
    c: DistanceY(g-1,g1) = 145
    c: DistanceY(g-1,g9) = 170
    c: Diameter(g11) = 1.71
    c: Diameter(g10) = 1.71
    c: Horizontal(g9,g0)
    c: Vertical(g0,g11)
    c: Horizontal(g10,g11)
    c: Vertical(g10,g9)
    c: DistanceY(g-1,g10) = 230
FEATURE [PartDesign::Hole] Hole002  label="Plate Connection Holes"
  BaseFeature = -> Mirrored
  CustomThreadClearance = 0
  Depth = 25
  DepthType = 0
  Diameter = 1.71
  DrillForDepth = false
  DrillPoint = 1
  DrillPointAngle = 118
  HoleCutCountersinkAngle = 90
  HoleCutCustomValues = false
  HoleCutDepth = 0
  HoleCutDiameter = 3.5
  HoleCutType = 2
  ModelThread = false
  Placement = pos=(0,0,0) rot=(1,0,0;1.5708rad)
  Profile = -> Sketch017
  Suppressed = false
  Tapered = false
  TaperedAngle = 90
  ThreadClass = 0
  ThreadDepth = 25
  ThreadDepthType = 0
  ThreadDirection = 0
  ThreadFit = 0
  ThreadSize = 0
  ThreadType = 0
  Threaded = false
  UseCustomThreadClearance = false
  expr: Diameter = <<Monitor Chassis Parameters>>.GSTowerLayerJoinScrewDiameter
  expr: HoleCutDiameter = <<Monitor Chassis Parameters>>.GSM2BoltCountersinkDiameter
FEATURE [Part::Part2DObjectPython] ShapeString  label="Orientation and ID ShapeString"  # Draft 2D object (typed FeaturePython)
  FontFile = <path>
  Fuse = false
  Justification = 6
  JustificationReference = 0
  KeepLeftMargin = false
  MakeFace = true
  ObliqueAngle = 0
  Placement = pos=(47.7,-0.7,4.8) rot=(0.57735,-0.57735,0.57735;2.0944rad)
  ScaleToSize = true
  Size = 5
  String = PiTrac                 --> UP                                                     --> UP
  Tracking = 0
FEATURE [PartDesign::Pocket] Pocket004  label="Orientation and ID Pocket"
  BaseFeature = -> Hole002
  Direction = (1e-16,1,-2e-16)
  Length = 1
  Length2 = 5
  Placement = pos=(0,0,0) rot=(1,0,0;1.5708rad)
  Profile = -> ShapeString
  ReferenceAxis = -> ShapeString [N_Axis]
  Suppressed = false
  Type = 0
FEATURE [PartDesign::Body] Body  label="Backplate Body - Compute Board Variant"
  AllowCompound = false
  Group = -> [Sketch,Sketch001,Pad,Pad001,Sketch002,Pad002,Sketch003,Hole,DatumPlane,Sketch004,Pad003,Mirrored,DatumPlane007,Sketch017,Hole002,ShapeString,Pocket004]
  Origin = -> Origin001
  Placement = pos=(0.2,-1,0) rot=(0,0,1;0rad)
  Tip = -> Pocket004
FEATURE [App::Part] Part  label="Tower Part"
  Group = -> [Body,Body001]
  Origin = -> Origin
note: 1 file-system path scrubbed to <path> (originals preserved in the JSON sidecar)
